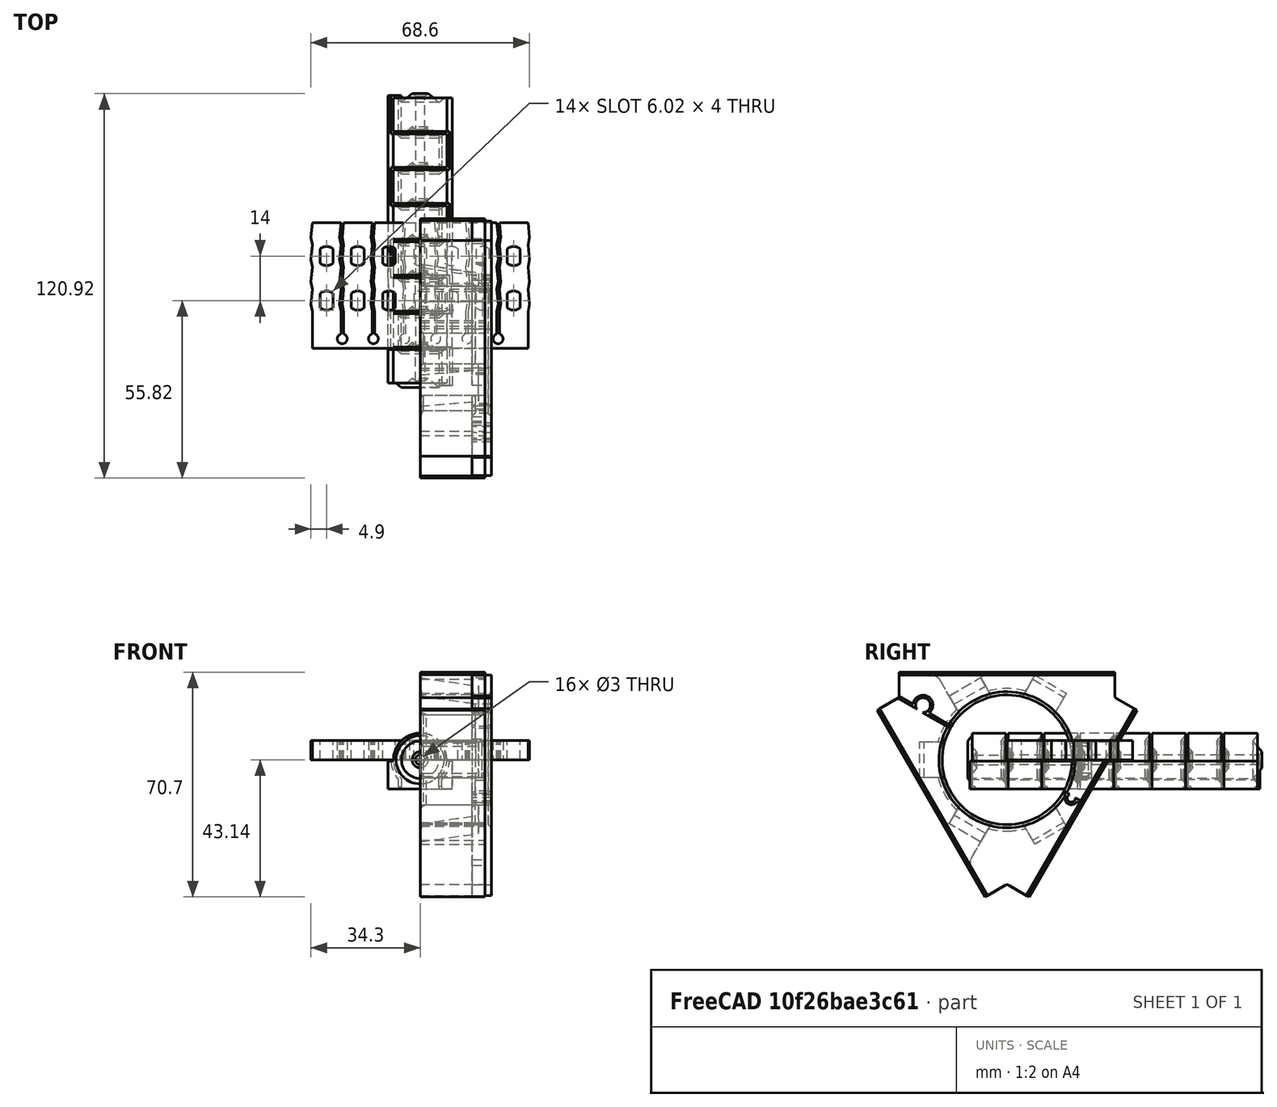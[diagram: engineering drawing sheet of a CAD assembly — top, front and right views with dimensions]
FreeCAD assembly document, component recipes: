
FREECAD ASSEMBLY — COMPONENT RECIPES ("BaseHingeModel_ver1.2-test")

This assembly document has 7 components, labeled P0..P6 below (a component is one placed body or linked part). 6 of them carry a construction recipe — the FreeCAD feature program that regenerates the part from scratch, quoted from this document or its linked companion documents; the rest are supplied as boundary geometry only. No exploded tour is included for this assembly.
COMPONENT P0 — geometry summary ("Assembly"; no construction recipe available for this part):
  bounding box: 98.9 x 69.8 x 17.6 mm
  tessellated surface: 7,914 triangles
  volume: 478904856520590368888311941004297705559593031450089613222557417315195802537240778087716927439343962383304309799745998996885905339609514451157107385303040 mm^3 (394367892825765304375067304335271323354279768632805773975574389521230489798256084268396323707668453363267439954332522702625322761590817962618779598848% of its bounding box)
COMPONENT P1 — recipe-attached ("BeamFixatoPart", modeled in this document).
Construction recipe (the document's own serialized feature program — sketch geometry with constraints, then the solid features built on it; lengths are millimeters unless a unit is written):

FEATURE [Sketcher::SketchObject] Sketch022  label="FixatorBodySketch"
  FullyConstrained = false
  MapMode = 5
  Support = -> [XY_Plane005]
  expr: Constraints[143] = Spreadsheet.mmCellWall
  expr: Constraints[144] = Spreadsheet.mmCellWall
  expr: Constraints[145] = Spreadsheet.mmCellWall
  expr: Constraints[146] = Spreadsheet.mmCellWidth
  expr: Constraints[147] = Spreadsheet.mmCellWidth
  expr: Constraints[148] = Spreadsheet.mmCellWidth
  expr: Constraints[169] = Spreadsheet.mmCommonBaseLenght
  expr: Constraints[170] = Spreadsheet.mmToothStep
  expr: Constraints[171] = Spreadsheet.mmToothStep
  expr: Constraints[172] = Spreadsheet.mmToothStep
  expr: Constraints[173] = Spreadsheet.mmToothStep
  expr: Constraints[174] = Spreadsheet.mmToothStep
  expr: Constraints[183] = Spreadsheet.mmCellWall * 3
  expr: Constraints[184] = Spreadsheet.mmCellWall * 3
  expr: Constraints[185] = Spreadsheet.mmCellWall * 3
  expr: Constraints[186] = Spreadsheet.mmCellWall * 3
  expr: Constraints[425] = Spreadsheet.mmFirstCircleArcToBase
  expr: Constraints[435] = Spreadsheet.mmCellWall / 2
  expr: Constraints[464] = Spreadsheet.mmCellWidth + Spreadsheet.mmCellWall
  expr: Constraints[5] = Spreadsheet.mmBaseWidth
  expr: Constraints[6] = Spreadsheet.mmBaseEnd
  sketch-geometry (155):
    g0: LineSegment StartX=-33.9 StartY=0 StartZ=0 EndX=-33.9 EndY=39.5 EndZ=0
    g1: LineSegment StartX=-33.9 StartY=39.5 StartZ=0 EndX=33.9 EndY=39.5 EndZ=0
    g2: LineSegment StartX=33.9 StartY=39.5 StartZ=0 EndX=33.9 EndY=0 EndZ=0
    g3: LineSegment StartX=-73.1099 StartY=25.5 StartZ=0 EndX=65.6354 EndY=25.5 EndZ=0
    g4: LineSegment StartX=-33.9 StartY=0 StartZ=0 EndX=-33.9 EndY=11.5 EndZ=0
    g5: LineSegment StartX=-33.9 StartY=11.5 StartZ=0 EndX=-34.3 EndY=13.9 EndZ=0
    g6: LineSegment StartX=-34.3 StartY=13.9 StartZ=0 EndX=-33.9 EndY=18.5 EndZ=0
    g7: LineSegment StartX=-33.9 StartY=18.5 StartZ=0 EndX=-34.3 EndY=20.9 EndZ=0
    g8: LineSegment StartX=-34.3 StartY=20.9 StartZ=0 EndX=-33.9 EndY=25.5 EndZ=0
    g9: LineSegment StartX=-33.9 StartY=25.5 StartZ=0 EndX=-34.3 EndY=27.9 EndZ=0
    g10: LineSegment StartX=-34.3 StartY=27.9 StartZ=0 EndX=-33.9 EndY=32.5 EndZ=0
    g11: LineSegment StartX=-33.9 StartY=32.5 StartZ=0 EndX=-34.3 EndY=34.9 EndZ=0
    g12: LineSegment StartX=-34.3 StartY=34.9 StartZ=0 EndX=-33.9 EndY=39.5 EndZ=0
    g13: LineSegment StartX=-33.9 StartY=39.5 StartZ=0 EndX=-24.9 EndY=39.5 EndZ=0
    g14: LineSegment StartX=-24.9 StartY=39.5 StartZ=0 EndX=-25.3 EndY=34.9 EndZ=0
    g15: LineSegment StartX=-25.3 StartY=34.9 StartZ=0 EndX=-24.9 EndY=32.5 EndZ=0
    g16: LineSegment StartX=-24.9 StartY=32.5 StartZ=0 EndX=-25.3 EndY=27.9 EndZ=0
    g17: LineSegment StartX=-25.3 StartY=27.9 StartZ=0 EndX=-24.9 EndY=25.5 EndZ=0
    g18: LineSegment StartX=-24.9 StartY=25.5 StartZ=0 EndX=-25.3 EndY=20.9 EndZ=0
    g19: LineSegment StartX=-25.3 StartY=20.9 StartZ=0 EndX=-24.9 EndY=18.5 EndZ=0
    g20: LineSegment StartX=-24.9 StartY=18.5 StartZ=0 EndX=-25.3 EndY=13.9 EndZ=0
    g21: LineSegment StartX=-25.3 StartY=13.9 StartZ=0 EndX=-24.9 EndY=11.5 EndZ=0
    g22: LineSegment StartX=-24.9 StartY=11.5 StartZ=0 EndX=-24.9 EndY=4.5 EndZ=0
    g23: LineSegment StartX=-24.1 StartY=4.5 StartZ=0 EndX=-24.1 EndY=11.5 EndZ=0
    g24: LineSegment StartX=-24.1 StartY=11.5 StartZ=0 EndX=-24.5 EndY=13.9 EndZ=0
    g25: LineSegment StartX=-24.5 StartY=13.9 StartZ=0 EndX=-24.1 EndY=18.5 EndZ=0
    g26: LineSegment StartX=-24.1 StartY=18.5 StartZ=0 EndX=-24.5 EndY=20.9 EndZ=0
    g27: LineSegment StartX=-24.5 StartY=20.9 StartZ=0 EndX=-24.1 EndY=25.5 EndZ=0
    g28: LineSegment StartX=-24.1 StartY=25.5 StartZ=0 EndX=-24.5 EndY=27.9 EndZ=0
    g29: LineSegment StartX=-24.5 StartY=27.9 StartZ=0 EndX=-24.1 EndY=32.5 EndZ=0
    g30: LineSegment StartX=-24.1 StartY=32.5 StartZ=0 EndX=-24.5 EndY=34.9 EndZ=0
    g31: LineSegment StartX=-24.5 StartY=34.9 StartZ=0 EndX=-24.1 EndY=39.5 EndZ=0
    g32: LineSegment StartX=-24.1 StartY=39.5 StartZ=0 EndX=-15.1 EndY=39.5 EndZ=0
    g33: LineSegment StartX=-15.1 StartY=39.5 StartZ=0 EndX=-15.5 EndY=34.9 EndZ=0
    g34: LineSegment StartX=-15.5 StartY=34.9 StartZ=0 EndX=-15.1 EndY=32.5 EndZ=0
    g35: LineSegment StartX=-15.1 StartY=32.5 StartZ=0 EndX=-15.5 EndY=27.9 EndZ=0
    g36: LineSegment StartX=-15.5 StartY=27.9 StartZ=0 EndX=-15.1 EndY=25.5 EndZ=0
    g37: LineSegment StartX=-15.1 StartY=25.5 StartZ=0 EndX=-15.5 EndY=20.9 EndZ=0
    g38: LineSegment StartX=-15.5 StartY=20.9 StartZ=0 EndX=-15.1 EndY=18.5 EndZ=0
    g39: LineSegment StartX=-15.1 StartY=18.5 StartZ=0 EndX=-15.5 EndY=13.9 EndZ=0
    g40: LineSegment StartX=-15.5 StartY=13.9 StartZ=0 EndX=-15.1 EndY=11.5 EndZ=0
    g41: LineSegment StartX=-15.1 StartY=11.5 StartZ=0 EndX=-15.1 EndY=4.5 EndZ=0
    g42: LineSegment StartX=-14.3 StartY=4.5 StartZ=0 EndX=-14.3 EndY=11.5 EndZ=0
    g43: LineSegment StartX=-14.3 StartY=11.5 StartZ=0 EndX=-14.7 EndY=13.9 EndZ=0
    g44: LineSegment StartX=-14.7 StartY=13.9 StartZ=0 EndX=-14.3 EndY=18.5 EndZ=0
    g45: LineSegment StartX=-14.3 StartY=18.5 StartZ=0 EndX=-14.7 EndY=20.9 EndZ=0
    g46: LineSegment StartX=-14.7 StartY=20.9 StartZ=0 EndX=-14.3 EndY=25.5 EndZ=0
    g47: LineSegment StartX=-14.3 StartY=25.5 StartZ=0 EndX=-14.7 EndY=27.9 EndZ=0
    g48: LineSegment StartX=-14.7 StartY=27.9 StartZ=0 EndX=-14.3 EndY=32.5 EndZ=0
    g49: LineSegment StartX=-14.3 StartY=32.5 StartZ=0 EndX=-14.7 EndY=34.9 EndZ=0
    g50: LineSegment StartX=-14.7 StartY=34.9 StartZ=0 EndX=-14.3 EndY=39.5 EndZ=0
    g51: LineSegment StartX=-14.3 StartY=39.5 StartZ=0 EndX=-5.3 EndY=39.5 EndZ=0
    g52: LineSegment StartX=-5.3 StartY=39.5 StartZ=0 EndX=-5.7 EndY=34.9 EndZ=0
    g53: LineSegment StartX=-5.7 StartY=34.9 StartZ=0 EndX=-5.3 EndY=32.5 EndZ=0
    g54: LineSegment StartX=-5.3 StartY=32.5 StartZ=0 EndX=-5.7 EndY=27.9 EndZ=0
    g55: LineSegment StartX=-5.7 StartY=27.9 StartZ=0 EndX=-5.3 EndY=25.5 EndZ=0
    g56: LineSegment StartX=-5.3 StartY=25.5 StartZ=0 EndX=-5.7 EndY=20.9 EndZ=0
    g57: LineSegment StartX=-5.7 StartY=20.9 StartZ=0 EndX=-5.3 EndY=18.5 EndZ=0
    g58: LineSegment StartX=-5.3 StartY=18.5 StartZ=0 EndX=-5.7 EndY=13.9 EndZ=0
    g59: LineSegment StartX=-5.7 StartY=13.9 StartZ=0 EndX=-5.3 EndY=11.5 EndZ=0
    g60: LineSegment StartX=-5.3 StartY=11.5 StartZ=0 EndX=-5.3 EndY=4.5 EndZ=0
    g61: LineSegment StartX=-4.5 StartY=4.5 StartZ=0 EndX=-4.5 EndY=11.5 EndZ=0
    g62: LineSegment StartX=-4.5 StartY=11.5 StartZ=0 EndX=-4.9 EndY=13.9 EndZ=0
    g63: LineSegment StartX=-4.9 StartY=13.9 StartZ=0 EndX=-4.5 EndY=18.5 EndZ=0
    g64: LineSegment StartX=-4.5 StartY=18.5 StartZ=0 EndX=-4.9 EndY=20.9 EndZ=0
    g65: LineSegment StartX=-4.9 StartY=20.9 StartZ=0 EndX=-4.5 EndY=25.5 EndZ=0
    g66: LineSegment StartX=-4.5 StartY=25.5 StartZ=0 EndX=-4.9 EndY=27.9 EndZ=0
    g67: LineSegment StartX=-4.9 StartY=27.9 StartZ=0 EndX=-4.5 EndY=32.5 EndZ=0
    g68: LineSegment StartX=-4.5 StartY=32.5 StartZ=0 EndX=-4.9 EndY=34.9 EndZ=0
    g69: LineSegment StartX=-4.9 StartY=34.9 StartZ=0 EndX=-4.5 EndY=39.5 EndZ=0
    g70: LineSegment StartX=-4.5 StartY=39.5 StartZ=0 EndX=4.5 EndY=39.5 EndZ=0
    g71: LineSegment StartX=4.5 StartY=39.5 StartZ=0 EndX=4.9 EndY=34.9 EndZ=0
    g72: LineSegment StartX=4.9 StartY=34.9 StartZ=0 EndX=4.5 EndY=32.5 EndZ=0
    g73: LineSegment StartX=4.5 StartY=32.5 StartZ=0 EndX=4.9 EndY=27.9 EndZ=0
    g74: LineSegment StartX=4.9 StartY=27.9 StartZ=0 EndX=4.5 EndY=25.5 EndZ=0
    g75: LineSegment StartX=4.5 StartY=25.5 StartZ=0 EndX=4.9 EndY=20.9 EndZ=0
    g76: LineSegment StartX=4.9 StartY=20.9 StartZ=0 EndX=4.5 EndY=18.5 EndZ=0
    g77: LineSegment StartX=4.5 StartY=18.5 StartZ=0 EndX=4.9 EndY=13.9 EndZ=0
    g78: LineSegment StartX=4.9 StartY=13.9 StartZ=0 EndX=4.5 EndY=11.5 EndZ=0
    g79: LineSegment StartX=4.5 StartY=11.5 StartZ=0 EndX=4.5 EndY=4.5 EndZ=0
    g80: LineSegment StartX=5.3 StartY=4.5 StartZ=0 EndX=5.3 EndY=11.5 EndZ=0
    g81: LineSegment StartX=5.3 StartY=11.5 StartZ=0 EndX=5.7 EndY=13.9 EndZ=0
    g82: LineSegment StartX=5.7 StartY=13.9 StartZ=0 EndX=5.3 EndY=18.5 EndZ=0
    g83: LineSegment StartX=5.3 StartY=18.5 StartZ=0 EndX=5.7 EndY=20.9 EndZ=0
    g84: LineSegment StartX=5.7 StartY=20.9 StartZ=0 EndX=5.3 EndY=25.5 EndZ=0
    g85: LineSegment StartX=5.3 StartY=25.5 StartZ=0 EndX=5.7 EndY=27.9 EndZ=0
    g86: LineSegment StartX=5.7 StartY=27.9 StartZ=0 EndX=5.3 EndY=32.5 EndZ=0
    g87: LineSegment StartX=5.3 StartY=32.5 StartZ=0 EndX=5.7 EndY=34.9 EndZ=0
    g88: LineSegment StartX=5.7 StartY=34.9 StartZ=0 EndX=5.3 EndY=39.5 EndZ=0
    g89: LineSegment StartX=5.3 StartY=39.5 StartZ=0 EndX=14.3 EndY=39.5 EndZ=0
    g90: LineSegment StartX=14.3 StartY=39.5 StartZ=0 EndX=14.7 EndY=34.9 EndZ=0
    g91: LineSegment StartX=14.7 StartY=34.9 StartZ=0 EndX=14.3 EndY=32.5 EndZ=0
    g92: LineSegment StartX=14.3 StartY=32.5 StartZ=0 EndX=14.7 EndY=27.9 EndZ=0
    g93: LineSegment StartX=14.7 StartY=27.9 StartZ=0 EndX=14.3 EndY=25.5 EndZ=0
    g94: LineSegment StartX=14.3 StartY=25.5 StartZ=0 EndX=14.7 EndY=20.9 EndZ=0
    g95: LineSegment StartX=14.7 StartY=20.9 StartZ=0 EndX=14.3 EndY=18.5 EndZ=0
    g96: LineSegment StartX=14.3 StartY=18.5 StartZ=0 EndX=14.7 EndY=13.9 EndZ=0
    g97: LineSegment StartX=14.7 StartY=13.9 StartZ=0 EndX=14.3 EndY=11.5 EndZ=0
    g98: LineSegment StartX=14.3 StartY=11.5 StartZ=0 EndX=14.3 EndY=4.5 EndZ=0
    g99: LineSegment StartX=15.1 StartY=4.5 StartZ=0 EndX=15.1 EndY=11.5 EndZ=0
    g100: LineSegment StartX=15.1 StartY=11.5 StartZ=0 EndX=15.5 EndY=13.9 EndZ=0
    g101: LineSegment StartX=15.5 StartY=13.9 StartZ=0 EndX=15.1 EndY=18.5 EndZ=0
    g102: LineSegment StartX=15.1 StartY=18.5 StartZ=0 EndX=15.5 EndY=20.9 EndZ=0
    g103: LineSegment StartX=15.5 StartY=20.9 StartZ=0 EndX=15.1 EndY=25.5 EndZ=0
    g104: LineSegment StartX=15.1 StartY=25.5 StartZ=0 EndX=15.5 EndY=27.9 EndZ=0
    g105: LineSegment StartX=15.5 StartY=27.9 StartZ=0 EndX=15.1 EndY=32.5 EndZ=0
    g106: LineSegment StartX=15.1 StartY=32.5 StartZ=0 EndX=15.5 EndY=34.9 EndZ=0
    g107: LineSegment StartX=15.5 StartY=34.9 StartZ=0 EndX=15.1 EndY=39.5 EndZ=0
    g108: LineSegment StartX=15.1 StartY=39.5 StartZ=0 EndX=24.1 EndY=39.5 EndZ=0
    g109: LineSegment StartX=24.1 StartY=39.5 StartZ=0 EndX=24.5 EndY=34.9 EndZ=0
    g110: LineSegment StartX=24.5 StartY=34.9 StartZ=0 EndX=24.1 EndY=32.5 EndZ=0
    g111: LineSegment StartX=24.1 StartY=32.5 StartZ=0 EndX=24.5 EndY=27.9 EndZ=0
    g112: LineSegment StartX=24.5 StartY=27.9 StartZ=0 EndX=24.1 EndY=25.5 EndZ=0
    g113: LineSegment StartX=24.1 StartY=25.5 StartZ=0 EndX=24.5 EndY=20.9 EndZ=0
    g114: LineSegment StartX=24.5 StartY=20.9 StartZ=0 EndX=24.1 EndY=18.5 EndZ=0
    g115: LineSegment StartX=24.1 StartY=18.5 StartZ=0 EndX=24.5 EndY=13.9 EndZ=0
    g116: LineSegment StartX=24.5 StartY=13.9 StartZ=0 EndX=24.1 EndY=11.5 EndZ=0
    g117: LineSegment StartX=24.1 StartY=11.5 StartZ=0 EndX=24.1 EndY=4.5 EndZ=0
    g118: LineSegment StartX=24.9 StartY=4.5 StartZ=0 EndX=24.9 EndY=11.5 EndZ=0
    g119: LineSegment StartX=24.9 StartY=11.5 StartZ=0 EndX=25.3 EndY=13.9 EndZ=0
    g120: LineSegment StartX=25.3 StartY=13.9 StartZ=0 EndX=24.9 EndY=18.5 EndZ=0
    g121: LineSegment StartX=24.9 StartY=18.5 StartZ=0 EndX=25.3 EndY=20.9 EndZ=0
    g122: LineSegment StartX=25.3 StartY=20.9 StartZ=0 EndX=24.9 EndY=25.5 EndZ=0
    g123: LineSegment StartX=24.9 StartY=25.5 StartZ=0 EndX=25.3 EndY=27.9 EndZ=0
    g124: LineSegment StartX=25.3 StartY=27.9 StartZ=0 EndX=24.9 EndY=32.5 EndZ=0
    g125: LineSegment StartX=24.9 StartY=32.5 StartZ=0 EndX=25.3 EndY=34.9 EndZ=0
    g126: LineSegment StartX=25.3 StartY=34.9 StartZ=0 EndX=24.9 EndY=39.5 EndZ=0
    g127: LineSegment StartX=24.9 StartY=39.5 StartZ=0 EndX=33.9 EndY=39.5 EndZ=0
    g128: LineSegment StartX=33.9 StartY=39.5 StartZ=0 EndX=34.3 EndY=34.9 EndZ=0
    g129: LineSegment StartX=34.3 StartY=34.9 StartZ=0 EndX=33.9 EndY=32.5 EndZ=0
    g130: LineSegment StartX=33.9 StartY=32.5 StartZ=0 EndX=34.3 EndY=27.9 EndZ=0
    g131: LineSegment StartX=34.3 StartY=27.9 StartZ=0 EndX=33.9 EndY=25.5 EndZ=0
    g132: LineSegment StartX=33.9 StartY=25.5 StartZ=0 EndX=34.3 EndY=20.9 EndZ=0
    g133: LineSegment StartX=34.3 StartY=20.9 StartZ=0 EndX=33.9 EndY=18.5 EndZ=0
    g134: LineSegment StartX=33.9 StartY=18.5 StartZ=0 EndX=34.3 EndY=13.9 EndZ=0
    g135: LineSegment StartX=34.3 StartY=13.9 StartZ=0 EndX=33.9 EndY=11.5 EndZ=0
    g136: LineSegment StartX=33.9 StartY=11.5 StartZ=0 EndX=33.9 EndY=0 EndZ=0
    g137: LineSegment StartX=33.9 StartY=0 StartZ=0 EndX=-33.9 EndY=0 EndZ=0
    g138: LineSegment StartX=-73.1099 StartY=18.5 StartZ=0 EndX=65.6354 EndY=18.5 EndZ=0
    g139: LineSegment StartX=-73.1099 StartY=34.9 StartZ=0 EndX=65.6354 EndY=34.9 EndZ=0
    g140: LineSegment StartX=-73.1099 StartY=32.5 StartZ=0 EndX=65.6354 EndY=32.5 EndZ=0
    g141: LineSegment StartX=-73.1099 StartY=27.9 StartZ=0 EndX=65.6354 EndY=27.9 EndZ=0
    g142: LineSegment StartX=-73.1099 StartY=20.9 StartZ=0 EndX=65.6354 EndY=20.9 EndZ=0
    g143: LineSegment StartX=-73.1099 StartY=11.5 StartZ=0 EndX=65.6354 EndY=11.5 EndZ=0
    g144: LineSegment StartX=-34.3 StartY=8.59208 StartZ=0 EndX=-34.3 EndY=49.4346 EndZ=0
    g145: LineSegment StartX=-73.1099 StartY=13.9 StartZ=0 EndX=65.6354 EndY=13.9 EndZ=0
    g146: LineSegment StartX=-33.9 StartY=0 StartZ=0 EndX=33.9 EndY=0 EndZ=0
    g147: LineSegment StartX=-73.1099 StartY=4.5 StartZ=0 EndX=65.6354 EndY=4.5 EndZ=0
    g148: ArcOfCircle CenterX=-24.5 CenterY=3 CenterZ=0 NormalX=0 NormalY=0 NormalZ=1 AngleXU=0 Radius=1.55242 StartAngle=1.8314 EndAngle=7.59338
    g149: ArcOfCircle CenterX=-14.7 CenterY=3 CenterZ=0 NormalX=0 NormalY=0 NormalZ=1 AngleXU=0 Radius=1.55242 StartAngle=1.8314 EndAngle=7.59338
    g150: ArcOfCircle CenterX=-4.9 CenterY=3 CenterZ=0 NormalX=0 NormalY=0 NormalZ=1 AngleXU=0 Radius=1.55242 StartAngle=1.8314 EndAngle=7.59338
    g151: ArcOfCircle CenterX=4.9 CenterY=3 CenterZ=0 NormalX=0 NormalY=0 NormalZ=1 AngleXU=0 Radius=1.55242 StartAngle=1.8314 EndAngle=7.59338
    g152: ArcOfCircle CenterX=14.7 CenterY=3 CenterZ=0 NormalX=0 NormalY=0 NormalZ=1 AngleXU=0 Radius=1.55242 StartAngle=1.8314 EndAngle=7.59338
    g153: ArcOfCircle CenterX=24.5 CenterY=3 CenterZ=0 NormalX=0 NormalY=0 NormalZ=1 AngleXU=0 Radius=1.55242 StartAngle=1.8314 EndAngle=7.59338
    g154: LineSegment StartX=-73.1099 StartY=3 StartZ=0 EndX=65.6354 EndY=3 EndZ=0
  constraints (469):
    c: Coincident(g0,g1)
    c: Coincident(g1,g2)
    c: Horizontal(g3)
    c: Symmetric(g0,g2,g-2)
    c: Symmetric(g1,g0,g-2)
    c: DistanceX(g0,g2) = 67.8
    c: DistanceX(g0,g1) = 67.8
    c: Coincident(g4,g5)
    c: Coincident(g5,g6)
    c: Coincident(g6,g7)
    c: Coincident(g7,g8)
    c: Coincident(g8,g9)
    c: Coincident(g9,g10)
    c: Coincident(g10,g11)
    c: Coincident(g11,g12)
    c: Coincident(g12,g13)
    c: Horizontal(g13)
    c: Coincident(g13,g14)
    c: Coincident(g14,g15)
    c: Coincident(g15,g16)
    c: Coincident(g16,g17)
    c: Coincident(g17,g18)
    c: Coincident(g18,g19)
    c: Coincident(g19,g20)
    c: Coincident(g20,g21)
    c: Coincident(g21,g22)
    c: Coincident(g23,g24)
    c: Coincident(g24,g25)
    c: Coincident(g25,g26)
    c: Coincident(g26,g27)
    c: Coincident(g27,g28)
    c: Coincident(g28,g29)
    c: Coincident(g29,g30)
    c: Coincident(g30,g31)
    c: Coincident(g31,g32)
    c: Horizontal(g32)
    c: Coincident(g32,g33)
    c: Coincident(g33,g34)
    c: Coincident(g34,g35)
    c: Coincident(g35,g36)
    c: Coincident(g36,g37)
    c: Coincident(g37,g38)
    c: Coincident(g38,g39)
    c: Coincident(g39,g40)
    c: Coincident(g40,g41)
    c: Coincident(g42,g43)
    c: Coincident(g43,g44)
    c: Coincident(g44,g45)
    c: Coincident(g45,g46)
    c: Coincident(g46,g47)
    c: Coincident(g47,g48)
    c: Coincident(g48,g49)
    c: Coincident(g49,g50)
    c: Coincident(g50,g51)
    c: Coincident(g51,g52)
    c: Coincident(g52,g53)
    c: Coincident(g53,g54)
    c: Coincident(g54,g55)
    c: Coincident(g55,g56)
    c: Coincident(g56,g57)
    c: Coincident(g57,g58)
    c: Coincident(g58,g59)
    c: Coincident(g59,g60)
    c: Coincident(g61,g62)
    c: Coincident(g62,g63)
    c: Coincident(g63,g64)
    c: Coincident(g64,g65)
    c: Coincident(g65,g66)
    c: Coincident(g66,g67)
    c: Coincident(g67,g68)
    c: Coincident(g68,g69)
    c: Coincident(g69,g70)
    c: Coincident(g70,g71)
    c: Coincident(g71,g72)
    c: Coincident(g72,g73)
    c: Coincident(g73,g74)
    c: Coincident(g74,g75)
    c: Coincident(g75,g76)
    c: Coincident(g76,g77)
    c: Coincident(g77,g78)
    c: Coincident(g78,g79)
    c: Coincident(g80,g81)
    c: Coincident(g81,g82)
    c: Coincident(g82,g83)
    c: Coincident(g83,g84)
    c: Coincident(g84,g85)
    c: Coincident(g85,g86)
    c: Coincident(g86,g87)
    c: Coincident(g87,g88)
    c: Coincident(g88,g89)
    c: Horizontal(g89)
    c: Coincident(g89,g90)
    c: Coincident(g90,g91)
    c: Coincident(g91,g92)
    c: Coincident(g92,g93)
    c: Coincident(g93,g94)
    c: Coincident(g94,g95)
    c: Coincident(g95,g96)
    c: Coincident(g96,g97)
    c: Coincident(g97,g98)
    c: Coincident(g99,g100)
    c: Coincident(g100,g101)
    c: Coincident(g101,g102)
    c: Coincident(g102,g103)
    c: Coincident(g103,g104)
    c: Coincident(g104,g105)
    c: Coincident(g105,g106)
    c: Coincident(g106,g107)
    c: Coincident(g107,g108)
    c: Coincident(g108,g109)
    c: Coincident(g109,g110)
    c: Coincident(g110,g111)
    c: Coincident(g111,g112)
    c: Coincident(g112,g113)
    c: Coincident(g113,g114)
    c: Coincident(g114,g115)
    c: Coincident(g115,g116)
    c: Coincident(g116,g117)
    c: Coincident(g118,g119)
    c: Coincident(g119,g120)
    c: Coincident(g120,g121)
    c: Coincident(g121,g122)
    c: Coincident(g122,g123)
    c: Coincident(g123,g124)
    c: Coincident(g124,g125)
    c: Coincident(g125,g126)
    c: Coincident(g126,g127)
    c: Coincident(g127,g128)
    c: Coincident(g128,g129)
    c: Coincident(g129,g130)
    c: Coincident(g130,g131)
    c: Coincident(g131,g132)
    c: Coincident(g132,g133)
    c: Coincident(g133,g134)
    c: Coincident(g134,g135)
    c: Coincident(g135,g136)
    c: Symmetric(g69,g70,g-2)
    c: Symmetric(g51,g88,g-2)
    c: Symmetric(g50,g89,g-2)
    c: Symmetric(g32,g107,g-2)
    c: Symmetric(g31,g108,g-2)
    c: Symmetric(g13,g126,g-2)
    c: Symmetric(g12,g127,g-2)
    c: DistanceX(g13,g31) = 0.8
    c: DistanceX(g32,g50) = 0.8
    c: DistanceX(g51,g69) = 0.8
    c: DistanceX(g13,g13) = 9
    c: DistanceX(g32,g32) = 9
    c: DistanceX(g51,g51) = 9
    c: Horizontal(g139)
    c: Horizontal(g140)
    c: Horizontal(g141)
    c: Horizontal(g142)
    c: Horizontal(g143)
    c: Vertical(g8,g6)
    c: Vertical(g6,g4)
    c: Vertical(g144)
    c: Horizontal(g145)
    c: Coincident(g146,g0)
    c: Coincident(g146,g2)
    c: Coincident(g0,g137)
    c: Coincident(g2,g137)
    c: Horizontal(g147)
    c: PointOnObject(g11,g139)
    c: PointOnObject(g11,g144)
    c: PointOnObject(g10,g140)
    c: PointOnObject(g9,g144)
    c: PointOnObject(g7,g142)
    c: Horizontal(g138)
    c: DistanceY(g137,g147) = 4.5
    c: DistanceY(g147,g143) = 7
    c: DistanceY(g143,g138) = 7
    c: DistanceY(g138,g3) = 7
    c: DistanceY(g3,g140) = 7
    c: DistanceY(g140,g0) = 7
    c: Vertical(g139,g140)
    c: Vertical(g140,g141)
    c: Vertical(g141,g3)
    c: Vertical(g3,g142)
    c: Vertical(g142,g138)
    c: Vertical(g138,g145)
    c: Vertical(g145,g143)
    c: Vertical(g143,g147)
    c: DistanceY(g143,g145) = 2.4
    c: DistanceY(g138,g142) = 2.4
    c: DistanceY(g3,g141) = 2.4
    c: DistanceY(g140,g139) = 2.4
    c: Parallel(g12,g14)
    c: Parallel(g11,g15)
    c: PointOnObject(g14,g139)
    c: PointOnObject(g30,g139)
    c: PointOnObject(g15,g140)
    c: PointOnObject(g29,g140)
    c: Parallel(g14,g31)
    c: PointOnObject(g16,g141)
    c: PointOnObject(g28,g141)
    c: PointOnObject(g17,g3)
    c: PointOnObject(g27,g3)
    c: PointOnObject(g18,g142)
    c: PointOnObject(g26,g142)
    c: PointOnObject(g19,g138)
    c: PointOnObject(g25,g138)
    c: PointOnObject(g20,g145)
    c: PointOnObject(g24,g145)
    c: PointOnObject(g21,g143)
    c: PointOnObject(g23,g143)
    c: PointOnObject(g22,g147)
    c: PointOnObject(g23,g147)
    c: PointOnObject(g33,g139)
    c: PointOnObject(g49,g139)
    c: PointOnObject(g52,g139)
    c: PointOnObject(g71,g139)
    c: PointOnObject(g87,g139)
    c: PointOnObject(g90,g139)
    c: PointOnObject(g106,g139)
    c: PointOnObject(g109,g139)
    c: PointOnObject(g125,g139)
    c: PointOnObject(g128,g139)
    c: PointOnObject(g34,g140)
    c: PointOnObject(g48,g140)
    c: PointOnObject(g53,g140)
    c: PointOnObject(g67,g140)
    c: PointOnObject(g72,g140)
    c: PointOnObject(g86,g140)
    c: PointOnObject(g91,g140)
    c: PointOnObject(g105,g140)
    c: PointOnObject(g110,g140)
    c: PointOnObject(g124,g140)
    c: PointOnObject(g129,g140)
    c: Parallel(g33,g50)
    c: Parallel(g52,g69)
    c: Parallel(g71,g88)
    c: Parallel(g71,g90)
    c: Parallel(g90,g107)
    c: Parallel(g71,g109)
    c: Parallel(g109,g126)
    c: Parallel(g126,g128)
    c: Symmetric(g71,g68,g-2)
    c: Symmetric(g72,g67,g-2)
    c: Vertical(g139,g140)
    c: Vertical(g140,g141)
    c: Vertical(g141,g3)
    c: Vertical(g3,g142)
    c: Vertical(g142,g138)
    c: Vertical(g138,g145)
    c: Vertical(g145,g143)
    c: Vertical(g143,g147)
    c: Parallel(g34,g49)
    c: Parallel(g49,g53)
    c: Parallel(g53,g68)
    c: Parallel(g35,g48)
    c: Parallel(g48,g54)
    c: Parallel(g54,g67)
    c: PointOnObject(g35,g141)
    c: PointOnObject(g47,g141)
    c: PointOnObject(g54,g141)
    c: PointOnObject(g66,g141)
    c: PointOnObject(g85,g141)
    c: PointOnObject(g92,g141)
    c: PointOnObject(g104,g141)
    c: PointOnObject(g111,g141)
    c: PointOnObject(g123,g141)
    c: PointOnObject(g130,g141)
    c: Symmetric(g66,g73,g-2)
    c: Symmetric(g65,g74,g-2)
    c: PointOnObject(g36,g3)
    c: PointOnObject(g46,g3)
    c: PointOnObject(g55,g3)
    c: PointOnObject(g65,g3)
    c: Parallel(g36,g47)
    c: Parallel(g47,g55)
    c: Parallel(g55,g66)
    c: Symmetric(g64,g75,g-2)
    c: Symmetric(g79,g61,g-2)
    c: Symmetric(g61,g78,g-2)
    c: Symmetric(g62,g77,g-2)
    c: Symmetric(g63,g76,g-2)
    c: Parallel(g37,g46)
    c: Parallel(g46,g56)
    c: Parallel(g56,g65)
    c: PointOnObject(g37,g142)
    c: PointOnObject(g45,g142)
    c: PointOnObject(g56,g142)
    c: PointOnObject(g64,g142)
    c: PointOnObject(g38,g138)
    c: PointOnObject(g44,g138)
    c: PointOnObject(g57,g138)
    c: PointOnObject(g63,g138)
    c: Parallel(g38,g45)
    c: Parallel(g45,g57)
    c: Parallel(g57,g64)
    c: PointOnObject(g39,g145)
    c: PointOnObject(g43,g145)
    c: PointOnObject(g58,g145)
    c: PointOnObject(g62,g145)
    c: Parallel(g39,g44)
    c: Parallel(g44,g58)
    c: Parallel(g58,g63)
    c: Parallel(g40,g43)
    c: Parallel(g43,g59)
    c: Parallel(g59,g62)
    c: PointOnObject(g40,g143)
    c: PointOnObject(g42,g143)
    c: PointOnObject(g59,g143)
    c: PointOnObject(g61,g143)
    c: PointOnObject(g41,g147)
    c: PointOnObject(g42,g147)
    c: PointOnObject(g60,g147)
    c: PointOnObject(g61,g147)
    c: Parallel(g41,g42)
    c: Parallel(g42,g60)
    c: Parallel(g60,g61)
    c: PointOnObject(g80,g147)
    c: PointOnObject(g98,g147)
    c: PointOnObject(g99,g147)
    c: PointOnObject(g117,g147)
    c: PointOnObject(g118,g147)
    c: PointOnObject(g80,g143)
    c: PointOnObject(g97,g143)
    c: PointOnObject(g99,g143)
    c: PointOnObject(g116,g143)
    c: PointOnObject(g118,g143)
    c: PointOnObject(g135,g143)
    c: Parallel(g79,g80)
    c: Parallel(g80,g98)
    c: Parallel(g98,g99)
    c: Parallel(g99,g117)
    c: Parallel(g117,g118)
    c: Parallel(g118,g136)
    c: Parallel(g72,g87)
    c: Parallel(g87,g91)
    c: Parallel(g91,g106)
    c: Parallel(g106,g110)
    c: Parallel(g110,g125)
    c: Parallel(g125,g129)
    c: Parallel(g73,g86)
    c: Parallel(g86,g92)
    c: Parallel(g92,g105)
    c: Parallel(g105,g111)
    c: Parallel(g111,g124)
    c: Parallel(g124,g130)
    c: PointOnObject(g84,g3)
    c: PointOnObject(g93,g3)
    c: PointOnObject(g103,g3)
    c: PointOnObject(g112,g3)
    c: PointOnObject(g122,g3)
    c: PointOnObject(g131,g3)
    c: Parallel(g74,g85)
    c: Parallel(g85,g93)
    c: Parallel(g93,g104)
    c: Parallel(g104,g112)
    c: Parallel(g112,g123)
    c: Parallel(g123,g131)
    c: PointOnObject(g83,g142)
    c: PointOnObject(g94,g142)
    c: PointOnObject(g102,g142)
    c: PointOnObject(g113,g142)
    c: PointOnObject(g121,g142)
    c: PointOnObject(g132,g142)
    c: Parallel(g75,g84)
    c: Parallel(g84,g94)
    c: Parallel(g94,g103)
    c: Parallel(g103,g113)
    c: Parallel(g113,g122)
    c: Parallel(g122,g132)
    c: PointOnObject(g82,g138)
    c: PointOnObject(g95,g138)
    c: PointOnObject(g101,g138)
    c: PointOnObject(g114,g138)
    c: PointOnObject(g120,g138)
    c: PointOnObject(g133,g138)
    c: PointOnObject(g81,g145)
    c: PointOnObject(g96,g145)
    c: PointOnObject(g100,g145)
    c: PointOnObject(g115,g145)
    c: PointOnObject(g119,g145)
    c: PointOnObject(g134,g145)
    c: Parallel(g76,g83)
    c: Parallel(g83,g95)
    c: Parallel(g95,g102)
    c: Parallel(g102,g114)
    c: Parallel(g114,g121)
    c: Parallel(g121,g133)
    c: Parallel(g77,g82)
    c: Parallel(g82,g96)
    c: Parallel(g96,g101)
    c: Parallel(g101,g115)
    c: Parallel(g115,g120)
    c: Parallel(g120,g134)
    c: Parallel(g78,g81)
    c: Parallel(g81,g97)
    c: Parallel(g97,g100)
    c: Parallel(g100,g116)
    c: Parallel(g116,g119)
    c: Parallel(g119,g135)
    c: DistanceY(g137,g-1) = 0
    c: PointOnObject(g148,g154)
    c: PointOnObject(g149,g154)
    c: PointOnObject(g150,g154)
    c: PointOnObject(g151,g154)
    c: PointOnObject(g152,g154)
    c: PointOnObject(g153,g154)
    c: PointOnObject(g22,g148)
    c: PointOnObject(g23,g148)
    c: PointOnObject(g41,g149)
    c: PointOnObject(g42,g149)
    c: PointOnObject(g60,g150)
    c: PointOnObject(g61,g150)
    c: PointOnObject(g79,g151)
    c: PointOnObject(g98,g152)
    c: PointOnObject(g99,g152)
    c: PointOnObject(g117,g153)
    c: PointOnObject(g118,g153)
    c: PointOnObject(g153,g147)
    c: PointOnObject(g153,g147)
    c: PointOnObject(g152,g147)
    c: PointOnObject(g152,g147)
    c: PointOnObject(g151,g147)
    c: PointOnObject(g151,g147)
    c: PointOnObject(g150,g147)
    c: PointOnObject(g150,g147)
    c: PointOnObject(g149,g147)
    c: PointOnObject(g149,g147)
    c: PointOnObject(g148,g147)
    c: PointOnObject(g148,g147)
    c: DistanceY(g154,g147) = 1.5
    c: Vertical(g147,g154)
    c: Vertical(g147,g154)
    c: Coincident(g136,g137)
    c: Coincident(g4,g137)
    c: Coincident(g0,g12)
    c: PointOnObject(g31,g1)
    c: PointOnObject(g50,g1)
    c: PointOnObject(g69,g1)
    c: PointOnObject(g6,g0)
    c: DistanceX(g144,g12) = 0.4
    c: PointOnObject(g9,g141)
    c: PointOnObject(g8,g3)
    c: PointOnObject(g7,g144)
    c: PointOnObject(g6,g138)
    c: PointOnObject(g5,g145)
    c: PointOnObject(g5,g144)
    c: PointOnObject(g4,g143)
    c: Parallel(g12,g33)
    c: Parallel(g12,g52)
    c: Parallel(g15,g30)
    c: Parallel(g11,g34)
    c: PointOnObject(g10,g0)
    c: Parallel(g16,g29)
    c: Parallel(g10,g16)
    c: Parallel(g10,g35)
    c: Parallel(g9,g17)
    c: Parallel(g17,g28)
    c: Parallel(g9,g36)
    c: Parallel(g18,g27)
    c: Parallel(g8,g18)
    c: Parallel(g8,g37)
    c: Parallel(g7,g19)
    c: Parallel(g19,g26)
    c: Parallel(g6,g20)
    c: Parallel(g20,g25)
    c: Parallel(g7,g38)
    c: Parallel(g6,g39)
    c: Symmetric(g150,g151,g-2)
    c: DistanceX(g150,g151) = 9.8
    c: Parallel(g23,g22)
    c: Parallel(g21,g24)
    c: Parallel(g5,g21)
    c: Parallel(g41,g23)
FEATURE [PartDesign::Pad] Pad  label="FixatorPadBody"
  Direction = (0,0,1)
  Length = 6
  Length2 = 10
  Profile = -> Sketch022
  ReferenceAxis = -> Sketch022 [N_Axis]
  Type = 0
  expr: Length = Spreadsheet.mmCellHight
FEATURE [Sketcher::SketchObject] Sketch  label="PiercesPocketSketch"
  AttachmentOffset = pos=(0,0,0) rot=(1,0,0;1.5708rad)
  FullyConstrained = true
  MapMode = 2
  Placement = pos=(0,0,0) rot=(0.707107,0.707107,0;3.14159rad)
  Support = -> [YZ_Plane005]
  expr: Constraints[108] = Spreadsheet.mmCellPierceWidth
  expr: Constraints[118] = Spreadsheet.mmCellPierceWidth
  expr: Constraints[128] = Spreadsheet.mmCellPierceWidth
  expr: Constraints[138] = Spreadsheet.mmCellPierceWidth
  expr: Constraints[148] = Spreadsheet.mmCellPierceWidth
  expr: Constraints[158] = Spreadsheet.mmCellPierceWidth
  expr: Constraints[171] = Spreadsheet.mmCellWidth + Spreadsheet.mmCellWall
  expr: Constraints[172] = Spreadsheet.mmCellWidth + Spreadsheet.mmCellWall
  expr: Constraints[173] = Spreadsheet.mmCellWidth + Spreadsheet.mmCellWall
  expr: Constraints[174] = Spreadsheet.mmCellWidth + Spreadsheet.mmCellWall
  expr: Constraints[175] = Spreadsheet.mmCellWidth + Spreadsheet.mmCellWall
  expr: Constraints[176] = Spreadsheet.mmCellWidth + Spreadsheet.mmCellWall
  expr: Constraints[178] = Spreadsheet.mmCellWidth / 2
  expr: Constraints[179] = Spreadsheet.mmCellWidth / 2
  expr: Constraints[180] = Spreadsheet.mmCommonBaseLenght + Spreadsheet.mmToothStep * 1.5
  expr: Constraints[181] = Spreadsheet.mmToothStep * 2
  expr: Constraints[19] = Spreadsheet.mmCellPierceWidth
  expr: Constraints[29] = Spreadsheet.mmCellPierceWidth
  expr: Constraints[39] = Spreadsheet.mmCellPierceWidth
  expr: Constraints[49] = Spreadsheet.mmCellPierceWidth
  expr: Constraints[59] = Spreadsheet.mmCellPierceWidth
  expr: Constraints[69] = Spreadsheet.mmCellPierceWidth
  expr: Constraints[82] = Spreadsheet.mmCellWidth + Spreadsheet.mmCellWall
  expr: Constraints[83] = Spreadsheet.mmCellWidth + Spreadsheet.mmCellWall
  expr: Constraints[84] = Spreadsheet.mmCellWidth + Spreadsheet.mmCellWall
  expr: Constraints[85] = Spreadsheet.mmCellWidth + Spreadsheet.mmCellWall
  expr: Constraints[86] = Spreadsheet.mmCellWidth + Spreadsheet.mmCellWall
  expr: Constraints[87] = Spreadsheet.mmCellWidth + Spreadsheet.mmCellWall
  expr: Constraints[98] = Spreadsheet.mmCellPierceWidth
  expr: Constraints[9] = Spreadsheet.mmCellPierceWidth
  sketch-geometry (56):
    g0: ArcOfCircle CenterX=29 CenterY=0 CenterZ=0 NormalX=0 NormalY=0 NormalZ=1 AngleXU=0 Radius=3.0104 StartAngle=2.41495 EndAngle=3.86823
    g1: LineSegment StartX=26.75 StartY=2 StartZ=0 EndX=31.25 EndY=2 EndZ=0
    g2: LineSegment StartX=26.75 StartY=-2 StartZ=0 EndX=31.25 EndY=-2 EndZ=0
    g3: ArcOfCircle CenterX=29 CenterY=0 CenterZ=0 NormalX=0 NormalY=0 NormalZ=1 AngleXU=0 Radius=3.0104 StartAngle=5.55654 EndAngle=7.00983
    g4: ArcOfCircle CenterX=29 CenterY=9.8 CenterZ=0 NormalX=0 NormalY=0 NormalZ=1 AngleXU=0 Radius=3.0104 StartAngle=2.41495 EndAngle=3.86823
    g5: LineSegment StartX=26.75 StartY=11.8 StartZ=0 EndX=31.25 EndY=11.8 EndZ=0
    g6: LineSegment StartX=26.75 StartY=7.8 StartZ=0 EndX=31.25 EndY=7.8 EndZ=0
    g7: ArcOfCircle CenterX=29 CenterY=9.8 CenterZ=0 NormalX=0 NormalY=0 NormalZ=1 AngleXU=0 Radius=3.0104 StartAngle=5.55654 EndAngle=7.00983
    g8: ArcOfCircle CenterX=29 CenterY=19.6 CenterZ=0 NormalX=0 NormalY=0 NormalZ=1 AngleXU=0 Radius=3.0104 StartAngle=2.41495 EndAngle=3.86823
    g9: LineSegment StartX=26.75 StartY=21.6 StartZ=0 EndX=31.25 EndY=21.6 EndZ=0
    g10: LineSegment StartX=26.75 StartY=17.6 StartZ=0 EndX=31.25 EndY=17.6 EndZ=0
    g11: ArcOfCircle CenterX=29 CenterY=19.6 CenterZ=0 NormalX=0 NormalY=0 NormalZ=1 AngleXU=0 Radius=3.0104 StartAngle=5.55654 EndAngle=7.00983
    g12: ArcOfCircle CenterX=29 CenterY=29.4 CenterZ=0 NormalX=0 NormalY=0 NormalZ=1 AngleXU=0 Radius=3.0104 StartAngle=2.41495 EndAngle=3.86823
    g13: LineSegment StartX=26.75 StartY=31.4 StartZ=0 EndX=31.25 EndY=31.4 EndZ=0
    g14: LineSegment StartX=26.75 StartY=27.4 StartZ=0 EndX=31.25 EndY=27.4 EndZ=0
    g15: ArcOfCircle CenterX=29 CenterY=29.4 CenterZ=0 NormalX=0 NormalY=0 NormalZ=1 AngleXU=0 Radius=3.0104 StartAngle=5.55654 EndAngle=7.00983
    g16: ArcOfCircle CenterX=29 CenterY=-9.8 CenterZ=0 NormalX=0 NormalY=0 NormalZ=1 AngleXU=0 Radius=3.0104 StartAngle=2.41495 EndAngle=3.86823
    g17: LineSegment StartX=26.75 StartY=-7.8 StartZ=0 EndX=31.25 EndY=-7.8 EndZ=0
    g18: LineSegment StartX=26.75 StartY=-11.8 StartZ=0 EndX=31.25 EndY=-11.8 EndZ=0
    g19: ArcOfCircle CenterX=29 CenterY=-9.8 CenterZ=0 NormalX=0 NormalY=0 NormalZ=1 AngleXU=0 Radius=3.0104 StartAngle=5.55654 EndAngle=7.00983
    g20: ArcOfCircle CenterX=29 CenterY=-19.6 CenterZ=0 NormalX=0 NormalY=0 NormalZ=1 AngleXU=0 Radius=3.0104 StartAngle=2.41495 EndAngle=3.86823
    g21: LineSegment StartX=26.75 StartY=-17.6 StartZ=0 EndX=31.25 EndY=-17.6 EndZ=0
    g22: LineSegment StartX=26.75 StartY=-21.6 StartZ=0 EndX=31.25 EndY=-21.6 EndZ=0
    g23: ArcOfCircle CenterX=29 CenterY=-19.6 CenterZ=0 NormalX=0 NormalY=0 NormalZ=1 AngleXU=0 Radius=3.0104 StartAngle=5.55654 EndAngle=7.00983
    g24: ArcOfCircle CenterX=29 CenterY=-29.4 CenterZ=0 NormalX=0 NormalY=0 NormalZ=1 AngleXU=0 Radius=3.0104 StartAngle=2.41495 EndAngle=3.86823
    g25: LineSegment StartX=26.75 StartY=-27.4 StartZ=0 EndX=31.25 EndY=-27.4 EndZ=0
    g26: LineSegment StartX=26.75 StartY=-31.4 StartZ=0 EndX=31.25 EndY=-31.4 EndZ=0
    g27: ArcOfCircle CenterX=29 CenterY=-29.4 CenterZ=0 NormalX=0 NormalY=0 NormalZ=1 AngleXU=0 Radius=3.0104 StartAngle=5.55654 EndAngle=7.00983
    g28: ArcOfCircle CenterX=15 CenterY=0 CenterZ=0 NormalX=0 NormalY=0 NormalZ=1 AngleXU=0 Radius=3.0104 StartAngle=2.41495 EndAngle=3.86823
    g29: LineSegment StartX=12.75 StartY=2 StartZ=0 EndX=17.25 EndY=2 EndZ=0
    g30: LineSegment StartX=12.75 StartY=-2 StartZ=0 EndX=17.25 EndY=-2 EndZ=0
    g31: ArcOfCircle CenterX=15 CenterY=0 CenterZ=0 NormalX=0 NormalY=0 NormalZ=1 AngleXU=0 Radius=3.0104 StartAngle=5.55654 EndAngle=7.00983
    g32: ArcOfCircle CenterX=15 CenterY=9.8 CenterZ=0 NormalX=0 NormalY=0 NormalZ=1 AngleXU=0 Radius=3.0104 StartAngle=2.41495 EndAngle=3.86823
    g33: LineSegment StartX=12.75 StartY=11.8 StartZ=0 EndX=17.25 EndY=11.8 EndZ=0
    g34: LineSegment StartX=12.75 StartY=7.8 StartZ=0 EndX=17.25 EndY=7.8 EndZ=0
    g35: ArcOfCircle CenterX=15 CenterY=9.8 CenterZ=0 NormalX=0 NormalY=0 NormalZ=1 AngleXU=0 Radius=3.0104 StartAngle=5.55654 EndAngle=7.00983
    g36: ArcOfCircle CenterX=15 CenterY=19.6 CenterZ=0 NormalX=0 NormalY=0 NormalZ=1 AngleXU=0 Radius=3.0104 StartAngle=2.41495 EndAngle=3.86823
    g37: LineSegment StartX=12.75 StartY=21.6 StartZ=0 EndX=17.25 EndY=21.6 EndZ=0
    g38: LineSegment StartX=12.75 StartY=17.6 StartZ=0 EndX=17.25 EndY=17.6 EndZ=0
    g39: ArcOfCircle CenterX=15 CenterY=19.6 CenterZ=0 NormalX=0 NormalY=0 NormalZ=1 AngleXU=0 Radius=3.0104 StartAngle=5.55654 EndAngle=7.00983
    g40: ArcOfCircle CenterX=15 CenterY=29.4 CenterZ=0 NormalX=0 NormalY=0 NormalZ=1 AngleXU=0 Radius=3.0104 StartAngle=2.41495 EndAngle=3.86823
    g41: LineSegment StartX=12.75 StartY=31.4 StartZ=0 EndX=17.25 EndY=31.4 EndZ=0
    g42: LineSegment StartX=12.75 StartY=27.4 StartZ=0 EndX=17.25 EndY=27.4 EndZ=0
    g43: ArcOfCircle CenterX=15 CenterY=29.4 CenterZ=0 NormalX=0 NormalY=0 NormalZ=1 AngleXU=0 Radius=3.0104 StartAngle=5.55654 EndAngle=7.00983
    g44: ArcOfCircle CenterX=15 CenterY=-9.8 CenterZ=0 NormalX=0 NormalY=0 NormalZ=1 AngleXU=0 Radius=3.0104 StartAngle=2.41495 EndAngle=3.86823
    g45: LineSegment StartX=12.75 StartY=-7.8 StartZ=0 EndX=17.25 EndY=-7.8 EndZ=0
    g46: LineSegment StartX=12.75 StartY=-11.8 StartZ=0 EndX=17.25 EndY=-11.8 EndZ=0
    g47: ArcOfCircle CenterX=15 CenterY=-9.8 CenterZ=0 NormalX=0 NormalY=0 NormalZ=1 AngleXU=0 Radius=3.0104 StartAngle=5.55654 EndAngle=7.00983
    g48: ArcOfCircle CenterX=15 CenterY=-19.6 CenterZ=0 NormalX=0 NormalY=0 NormalZ=1 AngleXU=0 Radius=3.0104 StartAngle=2.41495 EndAngle=3.86823
    g49: LineSegment StartX=12.75 StartY=-17.6 StartZ=0 EndX=17.25 EndY=-17.6 EndZ=0
    g50: LineSegment StartX=12.75 StartY=-21.6 StartZ=0 EndX=17.25 EndY=-21.6 EndZ=0
    g51: ArcOfCircle CenterX=15 CenterY=-19.6 CenterZ=0 NormalX=0 NormalY=0 NormalZ=1 AngleXU=0 Radius=3.0104 StartAngle=5.55654 EndAngle=7.00983
    g52: ArcOfCircle CenterX=15 CenterY=-29.4 CenterZ=0 NormalX=0 NormalY=0 NormalZ=1 AngleXU=0 Radius=3.0104 StartAngle=2.41495 EndAngle=3.86823
    g53: LineSegment StartX=12.75 StartY=-27.4 StartZ=0 EndX=17.25 EndY=-27.4 EndZ=0
    g54: LineSegment StartX=12.75 StartY=-31.4 StartZ=0 EndX=17.25 EndY=-31.4 EndZ=0
    g55: ArcOfCircle CenterX=15 CenterY=-29.4 CenterZ=0 NormalX=0 NormalY=0 NormalZ=1 AngleXU=0 Radius=3.0104 StartAngle=5.55654 EndAngle=7.00983
  constraints (182):
    c: Horizontal(g1)
    c: Horizontal(g2)
    c: PointOnObject(g1,g0)
    c: Coincident(g0,g3)
    c: Coincident(g0,g2)
    c: Coincident(g3,g2)
    c: Coincident(g1,g0)
    c: Coincident(g3,g1)
    c: Equal(g2,g1)
    c: DistanceY(g2,g1) = 4
    c: Horizontal(g5)
    c: Horizontal(g6)
    c: PointOnObject(g5,g4)
    c: Coincident(g4,g7)
    c: Coincident(g4,g6)
    c: Coincident(g7,g6)
    c: Coincident(g5,g4)
    c: Coincident(g7,g5)
    c: Equal(g6,g5)
    c: DistanceY(g6,g5) = 4
    c: Horizontal(g9)
    c: Horizontal(g10)
    c: PointOnObject(g9,g8)
    c: Coincident(g8,g11)
    c: Coincident(g8,g10)
    c: Coincident(g11,g10)
    c: Coincident(g9,g8)
    c: Coincident(g11,g9)
    c: Equal(g10,g9)
    c: DistanceY(g10,g9) = 4
    c: Horizontal(g13)
    c: Horizontal(g14)
    c: PointOnObject(g13,g12)
    c: Coincident(g12,g15)
    c: Coincident(g12,g14)
    c: Coincident(g15,g14)
    c: Coincident(g13,g12)
    c: Coincident(g15,g13)
    c: Equal(g14,g13)
    c: DistanceY(g14,g13) = 4
    c: Horizontal(g17)
    c: Horizontal(g18)
    c: PointOnObject(g17,g16)
    c: Coincident(g16,g19)
    c: Coincident(g16,g18)
    c: Coincident(g19,g18)
    c: Coincident(g17,g16)
    c: Coincident(g19,g17)
    c: Equal(g18,g17)
    c: DistanceY(g18,g17) = 4
    c: Horizontal(g21)
    c: Horizontal(g22)
    c: PointOnObject(g21,g20)
    c: Coincident(g20,g23)
    c: Coincident(g20,g22)
    c: Coincident(g23,g22)
    c: Coincident(g21,g20)
    c: Coincident(g23,g21)
    c: Equal(g22,g21)
    c: DistanceY(g22,g21) = 4
    c: Horizontal(g25)
    c: Horizontal(g26)
    c: PointOnObject(g25,g24)
    c: Coincident(g24,g27)
    c: Coincident(g24,g26)
    c: Coincident(g27,g26)
    c: Coincident(g25,g24)
    c: Coincident(g27,g25)
    c: Equal(g26,g25)
    c: DistanceY(g26,g25) = 4
    c: Vertical(g0,g4)
    c: Vertical(g4,g8)
    c: Vertical(g8,g12)
    c: Vertical(g12,g16)
    c: Vertical(g16,g20)
    c: Vertical(g20,g24)
    c: Equal(g2,g18)
    c: Equal(g18,g22)
    c: Equal(g22,g26)
    c: Equal(g1,g5)
    c: Equal(g5,g9)
    c: Equal(g9,g13)
    c: DistanceY(g8,g12) = 9.8
    c: DistanceY(g4,g8) = 9.8
    c: DistanceY(g0,g4) = 9.8
    c: DistanceY(g16,g0) = 9.8
    c: DistanceY(g20,g16) = 9.8
    c: DistanceY(g24,g20) = 9.8
    c: PointOnObject(g0,g-1)
    c: Horizontal(g29)
    c: Horizontal(g30)
    c: PointOnObject(g29,g28)
    c: Coincident(g28,g31)
    c: Coincident(g28,g30)
    c: Coincident(g31,g30)
    c: Coincident(g29,g28)
    c: Coincident(g31,g29)
    c: Equal(g30,g29)
    c: DistanceY(g30,g29) = 4
    c: Horizontal(g33)
    c: Horizontal(g34)
    c: PointOnObject(g33,g32)
    c: Coincident(g32,g35)
    c: Coincident(g32,g34)
    c: Coincident(g35,g34)
    c: Coincident(g33,g32)
    c: Coincident(g35,g33)
    c: Equal(g34,g33)
    c: DistanceY(g34,g33) = 4
    c: Horizontal(g37)
    c: Horizontal(g38)
    c: PointOnObject(g37,g36)
    c: Coincident(g36,g39)
    c: Coincident(g36,g38)
    c: Coincident(g39,g38)
    c: Coincident(g37,g36)
    c: Coincident(g39,g37)
    c: Equal(g38,g37)
    c: DistanceY(g38,g37) = 4
    c: Horizontal(g41)
    c: Horizontal(g42)
    c: PointOnObject(g41,g40)
    c: Coincident(g40,g43)
    c: Coincident(g40,g42)
    c: Coincident(g43,g42)
    c: Coincident(g41,g40)
    c: Coincident(g43,g41)
    c: Equal(g42,g41)
    c: DistanceY(g42,g41) = 4
    c: Horizontal(g45)
    c: Horizontal(g46)
    c: PointOnObject(g45,g44)
    c: Coincident(g44,g47)
    c: Coincident(g44,g46)
    c: Coincident(g47,g46)
    c: Coincident(g45,g44)
    c: Coincident(g47,g45)
    c: Equal(g46,g45)
    c: DistanceY(g46,g45) = 4
    c: Horizontal(g49)
    c: Horizontal(g50)
    c: PointOnObject(g49,g48)
    c: Coincident(g48,g51)
    c: Coincident(g48,g50)
    c: Coincident(g51,g50)
    c: Coincident(g49,g48)
    c: Coincident(g51,g49)
    c: Equal(g50,g49)
    c: DistanceY(g50,g49) = 4
    c: Horizontal(g53)
    c: Horizontal(g54)
    c: PointOnObject(g53,g52)
    c: Coincident(g52,g55)
    c: Coincident(g52,g54)
    c: Coincident(g55,g54)
    c: Coincident(g53,g52)
    c: Coincident(g55,g53)
    c: Equal(g54,g53)
    c: DistanceY(g54,g53) = 4
    c: Vertical(g28,g32)
    c: Vertical(g32,g36)
    c: Vertical(g36,g40)
    c: Vertical(g40,g44)
    c: Vertical(g44,g48)
    c: Vertical(g48,g52)
    c: Equal(g30,g46)
    c: Equal(g46,g50)
    c: Equal(g50,g54)
    c: Equal(g29,g33)
    c: Equal(g33,g37)
    c: Equal(g37,g41)
    c: DistanceY(g36,g40) = 9.8
    c: DistanceY(g32,g36) = 9.8
    c: DistanceY(g28,g32) = 9.8
    c: DistanceY(g44,g28) = 9.8
    c: DistanceY(g48,g44) = 9.8
    c: DistanceY(g52,g48) = 9.8
    c: PointOnObject(g28,g-1)
    c: DistanceX(g24,g26) = 4.5
    c: DistanceX(g52,g54) = 4.5
    c: DistanceX(g-1,g28) = 15
    c: DistanceX(g28,g0) = 14
FEATURE [PartDesign::Pocket] Pocket  label="PiercesPocket"
  BaseFeature = -> Pad
  Direction = (-2e-16,2e-16,1)
  Length = 69.4
  Length2 = 5
  Midplane = true
  Profile = -> Sketch
  ReferenceAxis = -> Sketch [N_Axis]
  Type = 0
  expr: Length = Spreadsheet.mmBaseWidth + Spreadsheet.mmCellWall * 2
FEATURE [PartDesign::Body] Body004  label="BeamFixator"
  Group = -> [Sketch022,Pad,Sketch,Pocket]
  Origin = -> Origin005
  Tip = -> Pocket
COMPONENT P2 — recipe-attached ("HingePart", modeled in this document).
Construction recipe (the document's own serialized feature program — sketch geometry with constraints, then the solid features built on it; lengths are millimeters unless a unit is written):

FEATURE [PartDesign::LinearPattern] LinearPattern
  Direction = -> Sketch007 [V_Axis]
  Length = 67.8
  Occurrences = 4
  Originals = -> [Revolution,Revolution004,Pocket001,Pocket002,Pad008,Pad009,Pad010,Pad011,Pocket004,Pocket005]
  expr: Length = Spreadsheet.mmHingeHight
  expr: Occurrences = Spreadsheet.nHingeHightDiskCnt
FEATURE [PartDesign::Body] Body005
  Group = -> [LinearPattern]
  Origin = -> Origin007
  Tip = -> LinearPattern
COMPONENT P3 — recipe-attached ("AxisFixatorPart", modeled in this document).
Construction recipe (the document's own serialized feature program — sketch geometry with constraints, then the solid features built on it; lengths are millimeters unless a unit is written):

FEATURE [Sketcher::SketchObject] Sketch027  label="CommonFixatorScatch"
  FullyConstrained = false
  MapMode = 5
  Placement = pos=(0,0,0) rot=(0.57735,0.57735,0.57735;2.0944rad)
  Support = -> [YZ_Plane013]
  expr: Constraints[0] = Spreadsheet.mmAxisTubeDia + 2 * Spreadsheet.mmFixatorThick + 2 * Spreadsheet.mmTwoSideTapeThick
  expr: Constraints[17] = Spreadsheet.mmAxisTubeDia / 2 + Spreadsheet.mmPetalHightMax + Spreadsheet.mmTwoSideTapeThick
  expr: Constraints[18] = Spreadsheet.mmAxisTubeDia / 2 + Spreadsheet.mmPetalHightMax + Spreadsheet.mmTwoSideTapeThick
  expr: Constraints[32] = Spreadsheet.mmPetalPocketWidth
  expr: Constraints[33] = Spreadsheet.mmBaseWidth
  expr: Constraints[3] = Spreadsheet.mmAxisTubeDia
  sketch-geometry (14):
    g0: Circle CenterX=0 CenterY=0 CenterZ=0 NormalX=0 NormalY=0 NormalZ=1 AngleXU=0 Radius=26.72
    g1: LineSegment StartX=0 StartY=0 StartZ=0 EndX=32.2586 EndY=18.6245 EndZ=0
    g2: ArcOfCircle CenterX=0 CenterY=0 CenterZ=0 NormalX=0 NormalY=0 NormalZ=1 AngleXU=0 Radius=20.4 StartAngle=5.32461 EndAngle=6.86682
    g3: LineSegment StartX=0 StartY=-20.4 StartZ=0 EndX=0 EndY=-39.1443 EndZ=0
    g4: LineSegment StartX=0 StartY=-39.1443 StartZ=0 EndX=6.1902 EndY=-42.7183 EndZ=0
    g5: LineSegment StartX=6.1902 StartY=-42.7183 StartZ=0 EndX=40.0902 EndY=15.9983 EndZ=0
    g6: LineSegment StartX=40.0902 StartY=15.9983 StartZ=0 EndX=33.9 EndY=19.5722 EndZ=0
    g7: LineSegment StartX=33.9 StartY=19.5722 StartZ=0 EndX=17.6669 EndY=10.2 EndZ=0
    g8: LineSegment StartX=14.7156 StartY=-14.1284 StartZ=0 EndX=17.9224 EndY=-19.6828 EndZ=0
    g9: LineSegment StartX=17.9224 StartY=-19.6828 StartZ=0 EndX=8.08455 EndY=-25.3627 EndZ=0
    g10: LineSegment StartX=8.08455 StartY=-25.3627 StartZ=0 EndX=4.87772 EndY=-19.8083 EndZ=0
    g11: ArcOfCircle CenterX=0 CenterY=0 CenterZ=0 NormalX=0 NormalY=0 NormalZ=1 AngleXU=0 Radius=20.4 StartAngle=4.71239 EndAngle=4.95383
    g12: ArcOfCircle CenterX=0 CenterY=0 CenterZ=0 NormalX=0 NormalY=0 NormalZ=1 AngleXU=0 Radius=20.4 StartAngle=5.51814 EndAngle=6.80678
    g13: LineSegment StartX=0 StartY=0 StartZ=0 EndX=18.7992 EndY=-32.5612 EndZ=0
  constraints (39):
    c: Diameter(g0) = 53.44
    c: Angle(g-1,g1) = 0.523599
    c: PointOnObject(g6,g1)
    c: Diameter(g2) = 40.8
    c: Vertical(g3)
    c: Coincident(g3,g4)
    c: Coincident(g4,g5)
    c: Coincident(g5,g6)
    c: Coincident(g6,g7)
    c: Coincident(g8,g9)
    c: Coincident(g9,g10)
    c: Equal(g2,g11)
    c: Coincident(g2,g11)
    c: PointOnObject(g3,g-2)
    c: Parallel(g4,g6)
    c: Perpendicular(g5,g4)
    c: Tangent(g0,g5)
    c: Distance(g8,g11) = 26.62
    c: Distance(g9,g11) = 26.62
    c: Coincident(g11,g12)
    c: PointOnObject(g7,g1)
    c: Coincident(g10,g11)
    c: Coincident(g11,g3)
    c: Coincident(g12,g8)
    c: PointOnObject(g12,g1)
    c: Coincident(g12,g7)
    c: PointOnObject(g7,g1)
    c: Perpendicular(g10,g9)
    c: Perpendicular(g9,g8)
    c: Coincident(g13,g11)
    c: Angle(g13,g-1) = 1.0472
    c: Symmetric(g10,g8,g13)
    c: Distance(g10,g8) = 11.3598
    c: Distance(g4,g5) = 67.8
    c: Equal(g4,g6)
    c: Equal(g3,g7)
    c: Coincident(g-1,g0)
    c: Coincident(g0,g11)
    c: Coincident(g11,g1)
FEATURE [PartDesign::Pad] Pad012  label="AxisFixatorBodyPad"
  Direction = (1,-2e-16,3e-16)
  Length = 20.4
  Length2 = 10
  Placement = pos=(0,0,0) rot=(0.57735,0.57735,0.57735;2.0944rad)
  Profile = -> Sketch027
  ReferenceAxis = -> Sketch027 [N_Axis]
  Type = 0
  expr: Length = Spreadsheet.mmFixatorHight
FEATURE [Sketcher::SketchObject] Sketch031  label="MaxPetalBase001"
  FullyConstrained = false
  MapMode = 5
  Placement = pos=(0,0,0) rot=(0.57735,0.57735,0.57735;2.0944rad)
  Support = -> [YZ_Plane013]
  expr: Constraints[0] = Spreadsheet.mmAxisTubeDia + 2 * Spreadsheet.mmFixatorThick
  expr: Constraints[10] = Spreadsheet.mmAxisTubeDia
  expr: Constraints[12] = Spreadsheet.mmPetalPocketWidth
  expr: Constraints[1] = Spreadsheet.mmAxisTubeDia
  expr: Constraints[6] = Spreadsheet.mmAxisTubeDia / 2 + Spreadsheet.mmPetalHightMax
  sketch-geometry (7):
    g0: Circle CenterX=0 CenterY=2.5e-15 CenterZ=0 NormalX=0 NormalY=0 NormalZ=1 AngleXU=0 Radius=39.855
    g1: Circle CenterX=0 CenterY=2.5e-15 CenterZ=0 NormalX=0 NormalY=0 NormalZ=1 AngleXU=0 Radius=26.62
    g2: ArcOfCircle CenterX=0 CenterY=2.5e-15 CenterZ=0 NormalX=0 NormalY=0 NormalZ=1 AngleXU=0 Radius=20.4 StartAngle=5.86056 EndAngle=6.76902
    g3: LineSegment StartX=19.5933 StartY=5.67991 StartZ=0 EndX=26.52 EndY=5.67991 EndZ=0
    g4: LineSegment StartX=26.52 StartY=5.67991 StartZ=0 EndX=26.52 EndY=-5.67991 EndZ=0
    g5: LineSegment StartX=26.52 StartY=-5.67991 StartZ=0 EndX=19.5933 EndY=-5.67991 EndZ=0
    g6: ArcOfCircle CenterX=0 CenterY=2.5e-15 CenterZ=0 NormalX=0 NormalY=0 NormalZ=1 AngleXU=0 Radius=20.4 StartAngle=6.00103 EndAngle=6.56534
  constraints (17):
    c: Diameter(g1) = 53.24
    c: Diameter(g2) = 40.8
    c: Coincident(g3,g4)
    c: Coincident(g4,g5)
    c: Coincident(g0,g2)
    c: Vertical(g4)
    c: DistanceX(g-1,g4) = 26.52
    c: Coincident(g6,g0)
    c: Coincident(g6,g3)
    c: Coincident(g6,g5)
    c: Diameter(g6) = 40.8
    c: Symmetric(g3,g5,g-1)
    c: DistanceY(g5,g3) = 11.3598
    c: Horizontal(g3)
    c: Horizontal(g5)
    c: Coincident(g1,g6)
    c: Coincident(g-1,g6)
FEATURE [Sketcher::SketchObject] Sketch032  label="MinPetalBase001"
  AttachmentOffset = pos=(0,0,18.36) rot=(0,0,1;0rad)
  FullyConstrained = false
  MapMode = 5
  Placement = pos=(18.36,-4.1e-15,4.1e-15) rot=(0.57735,0.57735,0.57735;2.0944rad)
  Support = -> [YZ_Plane013]
  expr: .AttachmentOffset.Base.z = Spreadsheet.mmFixatorHight * 0.9
  expr: Constraints[0] = Spreadsheet.mmAxisTubeDia + 2 * Spreadsheet.mmFixatorThick
  expr: Constraints[10] = Spreadsheet.mmAxisTubeDia
  expr: Constraints[12] = Spreadsheet.mmPetalPocketWidth
  expr: Constraints[1] = Spreadsheet.mmAxisTubeDia
  expr: Constraints[6] = Spreadsheet.mmAxisTubeDia / 2 + Spreadsheet.mmPetalHightMin
  sketch-geometry (7):
    g0: Circle CenterX=0 CenterY=2e-15 CenterZ=0 NormalX=0 NormalY=0 NormalZ=1 AngleXU=0 Radius=39.844
    g1: Circle CenterX=0 CenterY=2e-15 CenterZ=0 NormalX=0 NormalY=0 NormalZ=1 AngleXU=0 Radius=26.62
    g2: ArcOfCircle CenterX=0 CenterY=2e-15 CenterZ=0 NormalX=0 NormalY=0 NormalZ=1 AngleXU=0 Radius=20.4 StartAngle=3.89517 EndAngle=6.7757
    g3: LineSegment StartX=19.5933 StartY=5.67991 StartZ=0 EndX=23.46 EndY=5.67991 EndZ=0
    g4: LineSegment StartX=23.46 StartY=5.67991 StartZ=0 EndX=23.46 EndY=-5.67991 EndZ=0
    g5: LineSegment StartX=23.46 StartY=-5.67991 StartZ=0 EndX=19.5933 EndY=-5.67991 EndZ=0
    g6: ArcOfCircle CenterX=0 CenterY=2e-15 CenterZ=0 NormalX=0 NormalY=0 NormalZ=1 AngleXU=0 Radius=20.4 StartAngle=6.00103 EndAngle=6.56534
  constraints (17):
    c: Diameter(g1) = 53.24
    c: Diameter(g2) = 40.8
    c: Coincident(g3,g4)
    c: Coincident(g4,g5)
    c: Coincident(g0,g2)
    c: Vertical(g4)
    c: DistanceX(g-1,g4) = 23.46
    c: Coincident(g6,g0)
    c: Coincident(g6,g3)
    c: Coincident(g6,g5)
    c: Diameter(g6) = 40.8
    c: Symmetric(g3,g5,g-1)
    c: DistanceY(g5,g3) = 11.3598
    c: Horizontal(g5)
    c: Horizontal(g3)
    c: Coincident(g1,g6)
    c: Coincident(g-1,g6)
FEATURE [PartDesign::SubtractiveLoft] SubtractiveLoft  label="PetalBodySubtractiveLoft"
  BaseFeature = -> Pad012
  Closed = false
  Placement = pos=(0,0,0) rot=(0.57735,0.57735,0.57735;2.0944rad)
  Profile = -> Sketch031
  Ruled = false
  Sections = -> [Sketch032]
FEATURE [PartDesign::PolarPattern] PolarPattern  label="ExisFixatorBodyPolarPattern"
  Angle = 360
  Axis = -> Sketch027 [N_Axis]
  BaseFeature = -> SubtractiveLoft
  Occurrences = 3
  Originals = -> [Pad012,AdditiveLoft,SubtractiveLoft]
  Placement = pos=(0,0,0) rot=(0.57735,0.57735,0.57735;2.0944rad)
FEATURE [PartDesign::Chamfer] Chamfer001
  Angle = 45
  Base = -> PolarPattern [Edge38,Edge9,Edge5,Edge23,Edge65,Edge59,Edge69,Edge47,Edge41]
  BaseFeature = -> PolarPattern
  ChamferType = 1
  FlipDirection = false
  Placement = pos=(0,0,0) rot=(0.57735,0.57735,0.57735;2.0944rad)
  Size = 2
  Size2 = 1
  SupportTransform = false
  UseAllEdges = false
FEATURE [PartDesign::Body] Body007  label="AxisFixatorBody"
  Group = -> [Sketch027,Pad012,Sketch031,Sketch032,SubtractiveLoft,PolarPattern,Chamfer001]
  Origin = -> Origin013
  Tip = -> Chamfer001
COMPONENT P4 — recipe-attached ("PetalMountingTemplate", modeled in this document).
Construction recipe (the document's own serialized feature program — sketch geometry with constraints, then the solid features built on it; lengths are millimeters unless a unit is written):

FEATURE [Sketcher::SketchObject] Sketch035  label="CommonFixatorScatch001"
  AttachmentOffset = pos=(0,0,16.32) rot=(0,0,1;0rad)
  FullyConstrained = false
  MapMode = 5
  Placement = pos=(16.32,-3.6e-15,3.6e-15) rot=(0.57735,0.57735,0.57735;2.0944rad)
  Support = -> [YZ_Plane013]
  expr: .AttachmentOffset.Base.z = Spreadsheet.mmFixatorHight * 0.8
  expr: Constraints[0] = Spreadsheet.mmAxisTubeDia + 2 * Spreadsheet.mmFixatorThick
  expr: Constraints[24] = Spreadsheet.mmBaseWidth
  expr: Constraints[3] = Spreadsheet.mmAxisTubeDia
  sketch-geometry (9):
    g0: Circle CenterX=0 CenterY=0 CenterZ=0 NormalX=0 NormalY=0 NormalZ=1 AngleXU=0 Radius=26.62
    g1: LineSegment StartX=0 StartY=0 StartZ=0 EndX=49.303 EndY=28.4651 EndZ=0
    g2: ArcOfCircle CenterX=0 CenterY=0 CenterZ=0 NormalX=0 NormalY=0 NormalZ=1 AngleXU=0 Radius=20.4 StartAngle=4.71235 EndAngle=6.7955
    g3: LineSegment StartX=0 StartY=-20.4 StartZ=0 EndX=0 EndY=-39.1443 EndZ=0
    g4: LineSegment StartX=0 StartY=-39.1443 StartZ=0 EndX=6.1036 EndY=-42.6683 EndZ=0
    g5: LineSegment StartX=6.1036 StartY=-42.6683 StartZ=0 EndX=40.0036 EndY=16.0483 EndZ=0
    g6: LineSegment StartX=40.0036 StartY=16.0483 StartZ=0 EndX=33.9 EndY=19.5722 EndZ=0
    g7: LineSegment StartX=33.9 StartY=19.5722 StartZ=0 EndX=17.6669 EndY=10.2 EndZ=0
    g8: ArcOfCircle CenterX=0 CenterY=0 CenterZ=0 NormalX=0 NormalY=0 NormalZ=1 AngleXU=0 Radius=20.4 StartAngle=4.71239 EndAngle=6.80678
  constraints (25):
    c: Diameter(g0) = 53.24
    c: Angle(g-1,g1) = 0.523599
    c: PointOnObject(g6,g1)
    c: Diameter(g2) = 40.8
    c: Vertical(g3)
    c: Coincident(g3,g4)
    c: Coincident(g4,g5)
    c: Coincident(g5,g6)
    c: Coincident(g6,g7)
    c: PointOnObject(g3,g-2)
    c: Parallel(g4,g6)
    c: Perpendicular(g5,g4)
    c: Tangent(g0,g5)
    c: PointOnObject(g8,g1)
    c: Coincident(g8,g7)
    c: PointOnObject(g8,g-2)
    c: PointOnObject(g8,g-1)
    c: PointOnObject(g8,g2)
    c: Coincident(g3,g8)
    c: Equal(g4,g6)
    c: Equal(g7,g3)
    c: Coincident(g2,g1)
    c: Coincident(g8,g1)
    c: Coincident(g8,g0)
    c: Distance(g4,g5) = 67.8
FEATURE [PartDesign::Pad] Pad013  label="AxisFixatorBodyPad001"
  Direction = (1,-2e-16,3e-16)
  Length = 6.12
  Length2 = 10
  Placement = pos=(0,0,0) rot=(0.57735,0.57735,0.57735;2.0944rad)
  Profile = -> Sketch035
  ReferenceAxis = -> Sketch035 [N_Axis]
  Type = 0
  expr: Length = Spreadsheet.mmFixatorHight * 0.3
FEATURE [Sketcher::SketchObject] Sketch038  label="MaxPetalBase004"
  FullyConstrained = false
  MapMode = 5
  Placement = pos=(0,0,0) rot=(0.57735,0.57735,0.57735;2.0944rad)
  Support = -> [YZ_Plane013]
  expr: Constraints[0] = Spreadsheet.mmAxisTubeDia + 2 * Spreadsheet.mmFixatorThick
  expr: Constraints[10] = Spreadsheet.mmAxisTubeDia
  expr: Constraints[15] = Spreadsheet.mmPetalPocketWidth
  expr: Constraints[1] = Spreadsheet.mmAxisTubeDia
  expr: Constraints[6] = Spreadsheet.mmAxisTubeDia * 2
  sketch-geometry (7):
    g0: Circle CenterX=0 CenterY=2.5e-15 CenterZ=0 NormalX=0 NormalY=0 NormalZ=1 AngleXU=0 Radius=39.855
    g1: Circle CenterX=0 CenterY=-1.1e-15 CenterZ=0 NormalX=0 NormalY=0 NormalZ=1 AngleXU=0 Radius=26.62
    g2: ArcOfCircle CenterX=0 CenterY=2.5e-15 CenterZ=0 NormalX=0 NormalY=0 NormalZ=1 AngleXU=0 Radius=20.4 StartAngle=5.6709 EndAngle=6.80795
    g3: LineSegment StartX=19.5933 StartY=5.67991 StartZ=0 EndX=81.6 EndY=5.67991 EndZ=0
    g4: LineSegment StartX=81.6 StartY=5.67991 StartZ=0 EndX=81.6 EndY=-5.67991 EndZ=0
    g5: LineSegment StartX=81.6 StartY=-5.67991 StartZ=0 EndX=19.5933 EndY=-5.67991 EndZ=0
    g6: ArcOfCircle CenterX=0 CenterY=2.5e-15 CenterZ=0 NormalX=0 NormalY=0 NormalZ=1 AngleXU=0 Radius=20.4 StartAngle=6.00103 EndAngle=6.56534
  constraints (16):
    c: Diameter(g1) = 53.24
    c: Diameter(g2) = 40.8
    c: Coincident(g3,g4)
    c: Coincident(g4,g5)
    c: Coincident(g0,g2)
    c: Vertical(g4)
    c: DistanceX(g-1,g4) = 81.6
    c: Coincident(g6,g0)
    c: Coincident(g6,g3)
    c: Coincident(g6,g5)
    c: Diameter(g6) = 40.8
    c: Horizontal(g3)
    c: Horizontal(g5)
    c: PointOnObject(g6,g-2)
    c: Symmetric(g3,g5,g-1)
    c: DistanceY(g5,g3) = 11.3598
FEATURE [Sketcher::SketchObject] Sketch039  label="MinPetalBase003"
  AttachmentOffset = pos=(0,0,20.4) rot=(0,0,1;0rad)
  FullyConstrained = false
  MapMode = 5
  Placement = pos=(20.4,-4.5e-15,4.5e-15) rot=(0.57735,0.57735,0.57735;2.0944rad)
  Support = -> [YZ_Plane013]
  expr: .AttachmentOffset.Base.z = Spreadsheet.mmFixatorHight
  expr: Constraints[0] = Spreadsheet.mmAxisTubeDia + 2 * Spreadsheet.mmFixatorThick
  expr: Constraints[10] = Spreadsheet.mmAxisTubeDia
  expr: Constraints[11] = Spreadsheet.mmPetalPocketWidth
  expr: Constraints[1] = Spreadsheet.mmAxisTubeDia
  expr: Constraints[6] = Spreadsheet.mmAxisTubeDia * 2
  sketch-geometry (7):
    g0: Circle CenterX=0 CenterY=2.1e-15 CenterZ=0 NormalX=0 NormalY=0 NormalZ=1 AngleXU=0 Radius=39.844
    g1: Circle CenterX=0 CenterY=2.1e-15 CenterZ=0 NormalX=0 NormalY=0 NormalZ=1 AngleXU=0 Radius=26.62
    g2: ArcOfCircle CenterX=0 CenterY=2.1e-15 CenterZ=0 NormalX=0 NormalY=0 NormalZ=1 AngleXU=0 Radius=20.4 StartAngle=3.90517 EndAngle=6.76925
    g3: LineSegment StartX=19.5933 StartY=5.67991 StartZ=0 EndX=81.6 EndY=5.67991 EndZ=0
    g4: LineSegment StartX=81.6 StartY=5.67991 StartZ=0 EndX=81.6 EndY=-5.67991 EndZ=0
    g5: LineSegment StartX=81.6 StartY=-5.67991 StartZ=0 EndX=19.5933 EndY=-5.67991 EndZ=0
    g6: ArcOfCircle CenterX=0 CenterY=2.1e-15 CenterZ=0 NormalX=0 NormalY=0 NormalZ=1 AngleXU=0 Radius=20.4 StartAngle=6.00103 EndAngle=6.56534
  constraints (17):
    c: Diameter(g1) = 53.24
    c: Diameter(g2) = 40.8
    c: Coincident(g3,g4)
    c: Coincident(g4,g5)
    c: Coincident(g0,g2)
    c: Vertical(g4)
    c: DistanceX(g-1,g4) = 81.6
    c: Coincident(g6,g0)
    c: Coincident(g6,g3)
    c: Coincident(g6,g5)
    c: Diameter(g6) = 40.8
    c: DistanceY(g5,g3) = 11.3598
    c: Symmetric(g3,g5,g-1)
    c: Coincident(g1,g6)
    c: Coincident(g-1,g6)
    c: Horizontal(g3)
    c: Horizontal(g5)
FEATURE [PartDesign::SubtractiveLoft] SubtractiveLoft001  label="PetalBodySubtractiveLoft001"
  BaseFeature = -> Pad013
  Closed = false
  Placement = pos=(0,0,0) rot=(0.57735,0.57735,0.57735;2.0944rad)
  Profile = -> Sketch038
  Ruled = false
  Sections = -> [Sketch039]
FEATURE [PartDesign::PolarPattern] PolarPattern001  label="ExisFixatorBodyPolarPattern001"
  Angle = 360
  Axis = -> Sketch035 [N_Axis]
  BaseFeature = -> SubtractiveLoft001
  Occurrences = 3
  Originals = -> [Pad013,SubtractiveLoft001]
  Placement = pos=(0,0,0) rot=(0.57735,0.57735,0.57735;2.0944rad)
FEATURE [Sketcher::SketchObject] Sketch040  label="CommonFixatorScatch002"
  AttachmentOffset = pos=(0,0,16.32) rot=(0,0,1;0rad)
  FullyConstrained = true
  MapMode = 5
  Placement = pos=(16.32,-3.6e-15,3.6e-15) rot=(0.57735,0.57735,0.57735;2.0944rad)
  Support = -> [YZ_Plane013]
  expr: .AttachmentOffset.Base.z = Spreadsheet.mmFixatorHight * 0.8
  expr: Constraints[11] = Spreadsheet.mmAxisTubeDia * 2
  expr: Constraints[14] = Spreadsheet.mmTemplatePartsConnectorDia - 2 * Spreadsheet.mmAirSpace
  expr: Constraints[15] = Spreadsheet.mmTemplatePartsConnectorDia * 3 / 2
  expr: Constraints[1] = Spreadsheet.mmAxisTubeDia + 2 * Spreadsheet.mmFixatorThick
  expr: Constraints[27] = Spreadsheet.mmAirSpace
  expr: Constraints[33] = Spreadsheet.mmTemplatePartsConnectorDia / 3
  expr: Constraints[41] = Spreadsheet.mmTemplatePartsConnectorDia
  expr: Constraints[43] = Spreadsheet.mmTemplatePartsConnectorDia * 2 / 3
  expr: Constraints[45] = Spreadsheet.mmTemplatePartsConnectorDia * 2 / 3 - 2 * Spreadsheet.mmAirSpace
  expr: Constraints[52] = Spreadsheet.mmTemplatePartsConnectorDia / 3
  expr: Constraints[55] = Spreadsheet.mmTemplatePartsConnectorDia / 2
  sketch-geometry (19):
    g0: Circle CenterX=0 CenterY=0 CenterZ=0 NormalX=0 NormalY=0 NormalZ=1 AngleXU=0 Radius=40.8
    g1: Circle CenterX=0 CenterY=0 CenterZ=0 NormalX=0 NormalY=0 NormalZ=1 AngleXU=0 Radius=26.62
    g2: LineSegment StartX=-35.5321 StartY=20.0526 StartZ=0 EndX=-28.3499 EndY=15.9059 EndZ=0
    g3: LineSegment StartX=22.767 StartY=-13.6064 StartZ=0 EndX=23.167 EndY=-12.9136 EndZ=0
    g4: LineSegment StartX=23.167 StartY=-12.9136 StartZ=0 EndX=21.4554 EndY=-11.9254 EndZ=0
    g5: LineSegment StartX=-35.1321 StartY=20.7454 StartZ=0 EndX=-35.5321 EndY=20.0526 EndZ=0
    g6: LineSegment StartX=23.0536 StartY=-13.31 StartZ=0 EndX=-35.3338 EndY=20.4 EndZ=0
    g7: ArcOfCircle CenterX=-26.42 CenterY=17.1754 CenterZ=0 NormalX=0 NormalY=0 NormalZ=1 AngleXU=0 Radius=2.31 StartAngle=4.65418 EndAngle=10.0066
    g8: LineSegment StartX=-26.5543 StartY=14.8693 StartZ=0 EndX=18.3629 EndY=-11.0637 EndZ=0
    g9: LineSegment StartX=-29.5129 StartY=17.5011 StartZ=0 EndX=-35.1321 EndY=20.7454 EndZ=0
    g10: LineSegment StartX=-35.1321 StartY=20.7454 StartZ=0 EndX=-35.5321 EndY=20.0526 EndZ=0
    g11: LineSegment StartX=-35.5321 StartY=20.0526 StartZ=0 EndX=22.851 EndY=-13.6549 EndZ=0
    g12: LineSegment StartX=22.851 StartY=-13.6549 StartZ=0 EndX=23.251 EndY=-12.9621 EndZ=0
    g13: LineSegment StartX=23.251 StartY=-12.9621 StartZ=0 EndX=-35.1321 EndY=20.7454 EndZ=0
    g14: ArcOfCircle CenterX=-26.42 CenterY=17.1754 CenterZ=0 NormalX=0 NormalY=0 NormalZ=1 AngleXU=0 Radius=3.11 StartAngle=5.34093 EndAngle=9.31984
    g15: ArcOfCircle CenterX=20.188 CenterY=-12.0474 CenterZ=0 NormalX=0 NormalY=0 NormalZ=1 AngleXU=0 Radius=2.07333 StartAngle=2.64723 EndAngle=5.73035
    g16: ArcOfCircle CenterX=20.188 CenterY=-12.0474 CenterZ=0 NormalX=0 NormalY=0 NormalZ=1 AngleXU=0 Radius=1.27333 StartAngle=1.99844 EndAngle=6.37914
    g17: LineSegment StartX=21.9524 StartY=-13.1361 StartZ=0 EndX=22.767 EndY=-13.6064 EndZ=0
    g18: LineSegment StartX=19.6599 StartY=-10.8888 StartZ=0 EndX=-24.5914 EndY=14.6597 EndZ=0
  constraints (56):
    c: PointOnObject(g6,g0)
    c: Diameter(g1) = 53.24
    c: Coincident(g0,g1)
    c: Coincident(g0,g-1)
    c: Coincident(g3,g4)
    c: Coincident(g9,g5)
    c: Coincident(g5,g2)
    c: Perpendicular(g3,g2)
    c: Symmetric(g2,g9,g6)
    c: Symmetric(g17,g3,g6)
    c: PointOnObject(g0,g6)
    c: Diameter(g0) = 81.6
    c: PointOnObject(g6,g1)
    c: Angle(g-1,g6) = 2.61799
    c: Diameter(g7) = 4.62
    c: Distance(g7,g5) = 9.33
    c: Parallel(g9,g4)
    c: Parallel(g2,g8)
    c: Coincident(g10,g11)
    c: Coincident(g11,g12)
    c: Coincident(g12,g13)
    c: Coincident(g13,g10)
    c: PointOnObject(g10,g0)
    c: Symmetric(g10,g10,g6)
    c: Parallel(g6,g13)
    c: Parallel(g11,g13)
    c: Coincident(g5,g10)
    c: Distance(g3,g3) = 0.8
    c: Coincident(g3,g17)
    c: PointOnObject(g11,g1)
    c: PointOnObject(g12,g1)
    c: PointOnObject(g3,g13)
    c: Distance(g6,g3) = 0.1
    c: Distance(g2,g8) = 2.07333
    c: PointOnObject(g14,g13)
    c: PointOnObject(g14,g13)
    c: PointOnObject(g18,g14)
    c: PointOnObject(g9,g14)
    c: Coincident(g7,g8)
    c: Coincident(g7,g2)
    c: Coincident(g14,g7)
    c: Diameter(g14) = 6.22
    c: PointOnObject(g18,g13)
    c: Diameter(g15) = 4.14667
    c: Coincident(g15,g16)
    c: Diameter(g16) = 2.54667
    c: Coincident(g15,g8)
    c: PointOnObject(g8,g11)
    c: Coincident(g17,g15)
    c: PointOnObject(g15,g11)
    c: Coincident(g4,g16)
    c: Coincident(g18,g16)
    c: Distance(g16,g4) = 2.07333
    c: PointOnObject(g4,g13)
    c: PointOnObject(g16,g13)
    c: Distance(g15,g12) = 3.11
FEATURE [PartDesign::Pocket] Pocket003
  BaseFeature = -> PolarPattern001
  Direction = (-1,2e-16,-3e-16)
  Length = 40.8
  Length2 = 5
  Midplane = true
  Placement = pos=(0,0,0) rot=(0.57735,0.57735,0.57735;2.0944rad)
  Profile = -> Sketch040
  ReferenceAxis = -> Sketch040 [N_Axis]
  Type = 0
  expr: Length = Spreadsheet.mmAxisTubeDia
FEATURE [PartDesign::Chamfer] Chamfer002
  Angle = 45
  Base = -> Pocket003 [Edge1,Edge35,Edge31,Edge98,Edge94,Edge47,Edge12]
  BaseFeature = -> Pocket003
  ChamferType = 0
  FlipDirection = false
  Placement = pos=(0,0,0) rot=(0.57735,0.57735,0.57735;2.0944rad)
  Size = 1
  Size2 = 1
  SupportTransform = false
  UseAllEdges = false
FEATURE [PartDesign::Chamfer] Chamfer003
  Angle = 45
  Base = -> Chamfer002 [Edge56,Edge17,Edge3,Edge28]
  BaseFeature = -> Chamfer002
  ChamferType = 0
  FlipDirection = false
  Placement = pos=(0,0,0) rot=(0.57735,0.57735,0.57735;2.0944rad)
  Size = 1
  Size2 = 1
  SupportTransform = false
  UseAllEdges = false
FEATURE [PartDesign::Chamfer] Chamfer004
  Angle = 45
  Base = -> Chamfer003 [Edge56,Edge61,Edge130,Edge128,Edge73,Edge75]
  BaseFeature = -> Chamfer003
  ChamferType = 0
  FlipDirection = false
  Placement = pos=(0,0,0) rot=(0.57735,0.57735,0.57735;2.0944rad)
  Size = 1
  Size2 = 1
  SupportTransform = false
  UseAllEdges = false
FEATURE [PartDesign::Fillet] Fillet
  Base = -> Chamfer004 [Edge66,Edge26]
  BaseFeature = -> Chamfer004
  Placement = pos=(0,0,0) rot=(0.57735,0.57735,0.57735;2.0944rad)
  Radius = 1
  SupportTransform = false
  UseAllEdges = false
FEATURE [PartDesign::Body] Body010  label="AxisFixatorTemplate"
  Group = -> [Sketch035,Pad013,Sketch038,Sketch039,SubtractiveLoft001,PolarPattern001,Sketch040,Pocket003,Chamfer002,Chamfer003,Chamfer004,Fillet]
  Origin = -> Origin019
  Tip = -> Fillet
COMPONENT P5 — recipe-attached ("AxisFixatorAbsolete", modeled in this document).
Construction recipe (the document's own serialized feature program — sketch geometry with constraints, then the solid features built on it; lengths are millimeters unless a unit is written):

FEATURE [Sketcher::SketchObject] Sketch041  label="CommonFixatorScatch003"
  FullyConstrained = false
  MapMode = 5
  Placement = pos=(0,0,0) rot=(0.57735,0.57735,0.57735;2.0944rad)
  Support = -> [YZ_Plane013]
  expr: Constraints[22] = 2 * (Spreadsheet.mmAxisTubeDia / 2 + Spreadsheet.mmFixatorThick) / cos(Spreadsheet.angPetal / 2)
  expr: Constraints[23] = Spreadsheet.mmHingeHight
  expr: Constraints[31] = Spreadsheet.mmAxisTubeDia
  expr: Constraints[64] = Spreadsheet.mmPetalWidth + Spreadsheet.mmAirSpace
  expr: Constraints[67] = Spreadsheet.mmAxisTubeDia / 2 + Spreadsheet.mmPetalHightMax + Spreadsheet.mmTwoSideTapeThick + Spreadsheet.mmAirSpace
  sketch-geometry (24):
    g0: LineSegment StartX=33.9 StartY=19.5722 StartZ=0 EndX=-33.9 EndY=19.5722 EndZ=0
    g1: LineSegment StartX=-33.9 StartY=19.5722 StartZ=0 EndX=0 EndY=-39.1443 EndZ=0
    g2: LineSegment StartX=0 StartY=-39.1443 StartZ=0 EndX=33.9 EndY=19.5722 EndZ=0
    g3: Circle CenterX=0 CenterY=0 CenterZ=0 NormalX=0 NormalY=0 NormalZ=1 AngleXU=0 Radius=39.1443
    g4: LineSegment StartX=-23.8668 StartY=13.7795 StartZ=0 EndX=-23.8668 EndY=-13.7795 EndZ=0
    g5: LineSegment StartX=-23.8668 StartY=-13.7795 StartZ=0 EndX=0 EndY=-27.5591 EndZ=0
    g6: LineSegment StartX=0 StartY=-27.5591 StartZ=0 EndX=23.8668 EndY=-13.7795 EndZ=0
    g7: LineSegment StartX=23.8668 StartY=-13.7795 StartZ=0 EndX=23.8668 EndY=13.7795 EndZ=0
    g8: LineSegment StartX=23.8668 StartY=13.7795 StartZ=0 EndX=0 EndY=27.5591 EndZ=0
    g9: LineSegment StartX=-1e-16 StartY=27.5591 StartZ=0 EndX=-23.8668 EndY=13.7795 EndZ=0
    g10: Circle CenterX=0 CenterY=0 CenterZ=0 NormalX=0 NormalY=0 NormalZ=1 AngleXU=0 Radius=27.5591
    g11: LineSegment StartX=0 StartY=0 StartZ=0 EndX=33.9 EndY=19.5722 EndZ=0
    g12: ArcOfCircle CenterX=0 CenterY=0 CenterZ=0 NormalX=0 NormalY=0 NormalZ=1 AngleXU=0 Radius=20.4 StartAngle=4.5996 EndAngle=6.79538
    g13: LineSegment StartX=0 StartY=-20.4 StartZ=0 EndX=0 EndY=-39.1443 EndZ=0
    g14: LineSegment StartX=0 StartY=-39.1443 StartZ=0 EndX=6.91684 EndY=-43.1378 EndZ=0
    g15: LineSegment StartX=6.91684 StartY=-43.1378 StartZ=0 EndX=40.8168 EndY=15.5787 EndZ=0
    g16: LineSegment StartX=40.8168 StartY=15.5787 StartZ=0 EndX=33.9 EndY=19.5722 EndZ=0
    g17: LineSegment StartX=33.9 StartY=19.5722 StartZ=0 EndX=17.6669 EndY=10.2 EndZ=0
    g18: LineSegment StartX=14.7156 StartY=-14.1284 StartZ=0 EndX=18.6289 EndY=-20.9065 EndZ=0
    g19: LineSegment StartX=18.6289 StartY=-20.9065 StartZ=0 EndX=8.79105 EndY=-26.5864 EndZ=0
    g20: LineSegment StartX=8.79105 StartY=-26.5864 StartZ=0 EndX=4.87772 EndY=-19.8083 EndZ=0
    g21: ArcOfCircle CenterX=0 CenterY=0 CenterZ=0 NormalX=0 NormalY=0 NormalZ=1 AngleXU=0 Radius=20.4 StartAngle=4.71239 EndAngle=4.95383
    g22: ArcOfCircle CenterX=0 CenterY=0 CenterZ=0 NormalX=0 NormalY=0 NormalZ=1 AngleXU=0 Radius=20.4 StartAngle=5.51814 EndAngle=6.80678
    g23: LineSegment StartX=0 StartY=0 StartZ=0 EndX=19.5722 EndY=-33.9 EndZ=0
  constraints (64):
    c: Coincident(g0,g1)
    c: Coincident(g1,g2)
    c: Coincident(g2,g0)
    c: Equal(g0,g1)
    c: Equal(g0,g2)
    c: PointOnObject(g0,g3)
    c: Coincident(g4,g5)
    c: Coincident(g5,g6)
    c: Coincident(g6,g7)
    c: Coincident(g7,g8)
    c: Coincident(g8,g9)
    c: Coincident(g9,g4)
    c: Equal(g4, g5-g9) x5
    c: PointOnObject(g4,g10)
    c: PointOnObject(g5,g10)
    c: PointOnObject(g6,g10)
    c: PointOnObject(g7,g10)
    c: PointOnObject(g8,g10)
    c: Diameter(g10) = 55.1181
    c: Distance(g2) = 67.8
    c: PointOnObject(g5,g-2)
    c: PointOnObject(g4,g10)
    c: Angle(g-1,g11) = 0.523599
    c: Coincident(g3,g10)
    c: Coincident(g3,g11)
    c: Coincident(g3,g-1)
    c: PointOnObject(g0,g11)
    c: Diameter(g12) = 40.8
    c: Coincident(g12,g3)
    c: Vertical(g13)
    c: Coincident(g13,g14)
    c: Coincident(g14,g15)
    c: Coincident(g15,g16)
    c: Coincident(g16,g17)
    c: Coincident(g19,g20)
    c: Coincident(g1,g13)
    c: Coincident(g0,g16)
    c: Equal(g12,g21)
    c: Coincident(g12,g21)
    c: PointOnObject(g13,g-2)
    c: PointOnObject(g13,g3)
    c: Parallel(g2,g15)
    c: Parallel(g14,g16)
    c: Perpendicular(g15,g14)
    c: Tangent(g10,g15)
    c: PointOnObject(g11,g3)
    c: Coincident(g21,g22)
    c: PointOnObject(g17,g11)
    c: Coincident(g20,g21)
    c: Coincident(g21,g13)
    c: Coincident(g22,g18)
    c: PointOnObject(g22,g11)
    c: Coincident(g22,g17)
    c: PointOnObject(g17,g11)
    c: Perpendicular(g20,g19)
    c: Perpendicular(g19,g18)
    c: Coincident(g23,g21)
    c: Angle(g23,g-2) = 2.61799
    c: PointOnObject(g23,g3)
    c: Symmetric(g20,g18,g23)
    c: Distance(g20,g18) = 11.3598
    c: Perpendicular(g23,g19)
    c: Coincident(g18,g19)
    c: Distance(g21,g19) = 27.42
FEATURE [PartDesign::Pad] Pad014  label="AxisFixatorBodyPad002"
  Direction = (1,-2e-16,3e-16)
  Length = 20.4
  Length2 = 10
  Placement = pos=(0,0,0) rot=(0.57735,0.57735,0.57735;2.0944rad)
  Profile = -> Sketch041
  ReferenceAxis = -> Sketch041 [N_Axis]
  Type = 0
  expr: Length = Spreadsheet.mmFixatorHight
FEATURE [Sketcher::SketchObject] Sketch044  label="MaxPetalBase006"
  FullyConstrained = false
  MapMode = 5
  Placement = pos=(0,0,0) rot=(0.57735,0.57735,0.57735;2.0944rad)
  Support = -> [YZ_Plane013]
  expr: Constraints[0] = Spreadsheet.mmAxisTubeDia + 2 * Spreadsheet.mmFixatorThick
  expr: Constraints[14] = Spreadsheet.mmPetalWidth + Spreadsheet.mmAirSpace
  expr: Constraints[1] = Spreadsheet.mmAxisTubeDia
  expr: Constraints[5] = Spreadsheet.mmAxisTubeDia / 2 + Spreadsheet.mmPetalHightMax
  expr: Constraints[9] = Spreadsheet.mmAxisTubeDia
  sketch-geometry (7):
    g0: Circle CenterX=0 CenterY=0 CenterZ=0 NormalX=0 NormalY=0 NormalZ=1 AngleXU=0 Radius=39.855
    g1: Circle CenterX=0 CenterY=0 CenterZ=0 NormalX=0 NormalY=0 NormalZ=1 AngleXU=0 Radius=26.62
    g2: ArcOfCircle CenterX=0 CenterY=0 CenterZ=0 NormalX=0 NormalY=0 NormalZ=1 AngleXU=0 Radius=20.4 StartAngle=5.86249 EndAngle=6.74499
    g3: LineSegment StartX=19.5933 StartY=5.67991 StartZ=0 EndX=26.52 EndY=5.67991 EndZ=0
    g4: LineSegment StartX=26.52 StartY=5.67991 StartZ=0 EndX=26.52 EndY=-5.67991 EndZ=0
    g5: LineSegment StartX=26.52 StartY=-5.67991 StartZ=0 EndX=19.5933 EndY=-5.67991 EndZ=0
    g6: ArcOfCircle CenterX=0 CenterY=0 CenterZ=0 NormalX=0 NormalY=0 NormalZ=1 AngleXU=0 Radius=20.4 StartAngle=6.00103 EndAngle=6.56534
  constraints (22):
    c: Diameter(g1) = 53.24
    c: Diameter(g2) = 40.8
    c: Coincident(g3,g4)
    c: Coincident(g4,g5)
    c: Coincident(g0,g2)
    c: DistanceX(g-1,g4) = 26.52
    c: Coincident(g6,g0)
    c: Coincident(g6,g3)
    c: Coincident(g6,g5)
    c: Diameter(g6) = 40.8
    c: Coincident(g6,g-1)
    c: Symmetric(g3,g5,g-1)
    c: Horizontal(g5)
    c: Horizontal(g3)
    c: DistanceY(g5,g3) = 11.3598
    c: Coincident(g6,g1)
    c: PointOnObject(g6,g-2)
    c: PointOnObject(g6,g-1)
    c: PointOnObject(g6,g5)
    c: PointOnObject(g6,g3)
    c: PointOnObject(g3,g6)
    c: Vertical(g4)
FEATURE [Sketcher::SketchObject] Sketch045  label="MinPetalBase005"
  AttachmentOffset = pos=(0,0,18.36) rot=(0,0,1;0rad)
  FullyConstrained = false
  MapMode = 5
  Placement = pos=(18.36,-4.1e-15,4.1e-15) rot=(0.57735,0.57735,0.57735;2.0944rad)
  Support = -> [YZ_Plane013]
  expr: .AttachmentOffset.Base.z = Spreadsheet.mmFixatorHight * 0.9
  expr: Constraints[0] = Spreadsheet.mmAxisTubeDia + 2 * Spreadsheet.mmFixatorThick
  expr: Constraints[10] = Spreadsheet.mmAxisTubeDia
  expr: Constraints[12] = Spreadsheet.mmPetalWidth + Spreadsheet.mmAirSpace
  expr: Constraints[1] = Spreadsheet.mmAxisTubeDia
  expr: Constraints[6] = Spreadsheet.mmAxisTubeDia / 2 + Spreadsheet.mmPetalHightMin
  sketch-geometry (7):
    g0: Circle CenterX=0 CenterY=2.3e-15 CenterZ=0 NormalX=0 NormalY=0 NormalZ=1 AngleXU=0 Radius=39.844
    g1: Circle CenterX=0 CenterY=2.3e-15 CenterZ=0 NormalX=0 NormalY=0 NormalZ=1 AngleXU=0 Radius=26.62
    g2: ArcOfCircle CenterX=0 CenterY=2.3e-15 CenterZ=0 NormalX=0 NormalY=0 NormalZ=1 AngleXU=0 Radius=20.4 StartAngle=3.8687 EndAngle=6.82101
    g3: LineSegment StartX=19.5933 StartY=5.67991 StartZ=0 EndX=23.46 EndY=5.67991 EndZ=0
    g4: LineSegment StartX=23.46 StartY=5.67991 StartZ=0 EndX=23.46 EndY=-5.67991 EndZ=0
    g5: LineSegment StartX=23.46 StartY=-5.67991 StartZ=0 EndX=19.5933 EndY=-5.67991 EndZ=0
    g6: ArcOfCircle CenterX=0 CenterY=2.3e-15 CenterZ=0 NormalX=0 NormalY=0 NormalZ=1 AngleXU=0 Radius=20.4 StartAngle=6.00103 EndAngle=6.56534
  constraints (17):
    c: Diameter(g1) = 53.24
    c: Diameter(g2) = 40.8
    c: Coincident(g3,g4)
    c: Coincident(g4,g5)
    c: Coincident(g0,g2)
    c: Vertical(g4)
    c: DistanceX(g-1,g4) = 23.46
    c: Coincident(g6,g0)
    c: Coincident(g6,g3)
    c: Coincident(g6,g5)
    c: Diameter(g6) = 40.8
    c: Symmetric(g3,g5,g-1)
    c: DistanceY(g5,g3) = 11.3598
    c: Horizontal(g3)
    c: Horizontal(g5)
    c: Coincident(g6,g1)
    c: Coincident(g6,g-1)
FEATURE [PartDesign::SubtractiveLoft] SubtractiveLoft002  label="PetalBodySubtractiveLoft002"
  BaseFeature = -> Pad014
  Closed = false
  Placement = pos=(0,0,0) rot=(0.57735,0.57735,0.57735;2.0944rad)
  Profile = -> Sketch044
  Ruled = false
  Sections = -> [Sketch045]
FEATURE [PartDesign::PolarPattern] PolarPattern002  label="ExisFixatorBodyPolarPattern002"
  Angle = 360
  Axis = -> Sketch041 [N_Axis]
  BaseFeature = -> SubtractiveLoft002
  Occurrences = 3
  Originals = -> [Pad014,SubtractiveLoft002]
  Placement = pos=(0,0,0) rot=(0.57735,0.57735,0.57735;2.0944rad)
FEATURE [PartDesign::Body] Body011  label="AxisFixatorBody001"
  Group = -> [Sketch041,Pad014,Sketch044,Sketch045,SubtractiveLoft002,PolarPattern002]
  Origin = -> Origin021
  Tip = -> PolarPattern002
COMPONENT P6 — recipe-attached ("PetalPart", modeled in this document).
Construction recipe (the document's own serialized feature program — sketch geometry with constraints, then the solid features built on it; lengths are millimeters unless a unit is written):

FEATURE [Sketcher::SketchObject] Sketch029  label="MaxPetalBase"
  FullyConstrained = false
  MapMode = 5
  Placement = pos=(0,0,0) rot=(0.57735,0.57735,0.57735;2.0944rad)
  Support = -> [YZ_Plane015]
  expr: Constraints[0] = Spreadsheet.mmAxisTubeDia + 2 * Spreadsheet.mmFixatorThick
  expr: Constraints[12] = Spreadsheet.mmAxisTubeDia / 2 + Spreadsheet.mmPetalHightMax
  expr: Constraints[16] = Spreadsheet.mmPetalWidth
  expr: Constraints[1] = Spreadsheet.mmAxisTubeDia
  expr: Constraints[6] = Spreadsheet.mmAxisTubeDia + Spreadsheet.mmTwoSideTapeThick * 2
  sketch-geometry (7):
    g0: Circle CenterX=0 CenterY=0 CenterZ=0 NormalX=0 NormalY=0 NormalZ=1 AngleXU=0 Radius=39.8652
    g1: Circle CenterX=0 CenterY=0 CenterZ=0 NormalX=0 NormalY=0 NormalZ=1 AngleXU=0 Radius=26.62
    g2: ArcOfCircle CenterX=0 CenterY=0 CenterZ=0 NormalX=0 NormalY=0 NormalZ=1 AngleXU=0 Radius=20.4 StartAngle=3.89684 EndAngle=6.80091
    g3: LineSegment StartX=19.8084 StartY=5.27991 StartZ=0 EndX=26.52 EndY=5.27991 EndZ=0
    g4: LineSegment StartX=26.52 StartY=5.27991 StartZ=0 EndX=26.52 EndY=-5.27991 EndZ=0
    g5: LineSegment StartX=26.52 StartY=-5.27991 StartZ=0 EndX=19.8084 EndY=-5.27991 EndZ=0
    g6: ArcOfCircle CenterX=0 CenterY=0 CenterZ=0 NormalX=0 NormalY=0 NormalZ=1 AngleXU=0 Radius=20.5 StartAngle=6.02269 EndAngle=6.54368
  constraints (20):
    c: Diameter(g1) = 53.24
    c: Diameter(g2) = 40.8
    c: Coincident(g3,g4)
    c: Coincident(g4,g5)
    c: PointOnObject(g3,g2)
    c: Coincident(g6,g0)
    c: Diameter(g6) = 41
    c: Coincident(g1,g6)
    c: Coincident(g0,g2)
    c: Vertical(g4)
    c: PointOnObject(g3,g6)
    c: PointOnObject(g5,g6)
    c: DistanceX(g-1,g4) = 26.52
    c: Horizontal(g3)
    c: Horizontal(g5)
    c: Symmetric(g5,g3,g-1)
    c: DistanceY(g5,g3) = 10.5598
    c: Coincident(g-1,g6)
    c: PointOnObject(g6,g5)
    c: PointOnObject(g6,g3)
FEATURE [Sketcher::SketchObject] Sketch030  label="MinPetalBase"
  AttachmentOffset = pos=(0,0,20.4) rot=(0,0,1;0rad)
  FullyConstrained = false
  MapMode = 5
  Placement = pos=(20.4,-4.5e-15,4.5e-15) rot=(0.57735,0.57735,0.57735;2.0944rad)
  Support = -> [YZ_Plane015]
  expr: .AttachmentOffset.Base.z = Spreadsheet.mmFixatorHight
  expr: Constraints[0] = Spreadsheet.mmAxisTubeDia + 2 * Spreadsheet.mmFixatorThick
  expr: Constraints[11] = Spreadsheet.mmAxisTubeDia / 2 + Spreadsheet.mmPetalHightMin
  expr: Constraints[15] = Spreadsheet.mmPetalWidth
  expr: Constraints[1] = Spreadsheet.mmAxisTubeDia
  expr: Constraints[5] = Spreadsheet.mmAxisTubeDia + Spreadsheet.mmTwoSideTapeThick * 2
  sketch-geometry (7):
    g0: Circle CenterX=0 CenterY=1.8e-15 CenterZ=0 NormalX=0 NormalY=0 NormalZ=1 AngleXU=0 Radius=39.865
    g1: Circle CenterX=0 CenterY=1.8e-15 CenterZ=0 NormalX=0 NormalY=0 NormalZ=1 AngleXU=0 Radius=26.62
    g2: ArcOfCircle CenterX=0 CenterY=1.8e-15 CenterZ=0 NormalX=0 NormalY=0 NormalZ=1 AngleXU=0 Radius=20.4 StartAngle=3.86544 EndAngle=6.7404
    g3: LineSegment StartX=19.8084 StartY=5.27991 StartZ=0 EndX=23.46 EndY=5.27991 EndZ=0
    g4: LineSegment StartX=23.46 StartY=5.27991 StartZ=0 EndX=23.46 EndY=-5.27991 EndZ=0
    g5: LineSegment StartX=23.46 StartY=-5.27991 StartZ=0 EndX=19.8084 EndY=-5.27991 EndZ=0
    g6: ArcOfCircle CenterX=0 CenterY=1.8e-15 CenterZ=0 NormalX=0 NormalY=0 NormalZ=1 AngleXU=0 Radius=20.5 StartAngle=6.02269 EndAngle=6.54368
  constraints (20):
    c: Diameter(g1) = 53.24
    c: Diameter(g2) = 40.8
    c: Coincident(g3,g4)
    c: Coincident(g4,g5)
    c: Coincident(g6,g0)
    c: Diameter(g6) = 41
    c: Coincident(g1,g6)
    c: Coincident(g0,g2)
    c: Vertical(g4)
    c: PointOnObject(g3,g6)
    c: PointOnObject(g5,g6)
    c: DistanceX(g-1,g4) = 23.46
    c: PointOnObject(g6,g5)
    c: PointOnObject(g6,g3)
    c: Coincident(g6,g-1)
    c: DistanceY(g5,g3) = 10.5598
    c: Symmetric(g5,g3,g-1)
    c: Horizontal(g3)
    c: Horizontal(g5)
    c: PointOnObject(g6,g-2)
FEATURE [PartDesign::AdditiveLoft] AdditiveLoft  label="PetalBodyBodyAdditiveLoft"
  Closed = false
  Placement = pos=(0,0,0) rot=(0.57735,0.57735,0.57735;2.0944rad)
  Profile = -> Sketch029
  Ruled = false
  Sections = -> [Sketch030]
FEATURE [PartDesign::Chamfer] Chamfer
  Angle = 45
  Base = -> AdditiveLoft [Edge8,Edge9,Edge6,Edge3,Edge2,Edge1,Edge11,Edge5]
  BaseFeature = -> AdditiveLoft
  ChamferType = 0
  FlipDirection = false
  Placement = pos=(0,0,0) rot=(0.57735,0.57735,0.57735;2.0944rad)
  Size = 1
  Size2 = 1
  SupportTransform = false
  UseAllEdges = false
FEATURE [PartDesign::Body] Body008  label="PetalBodyPart"
  Group = -> [Sketch029,Sketch030,AdditiveLoft,Chamfer]
  Origin = -> Origin015
  Tip = -> Chamfer
PROVENANCE & LICENSES
A FreeCAD (.FCStd) document from a public repository crawl; recipes are the document's own serialized feature recipes (and, for linked parts, companion documents' recipes).
License: as declared in the source repository (recorded in the dataset sidecar).
